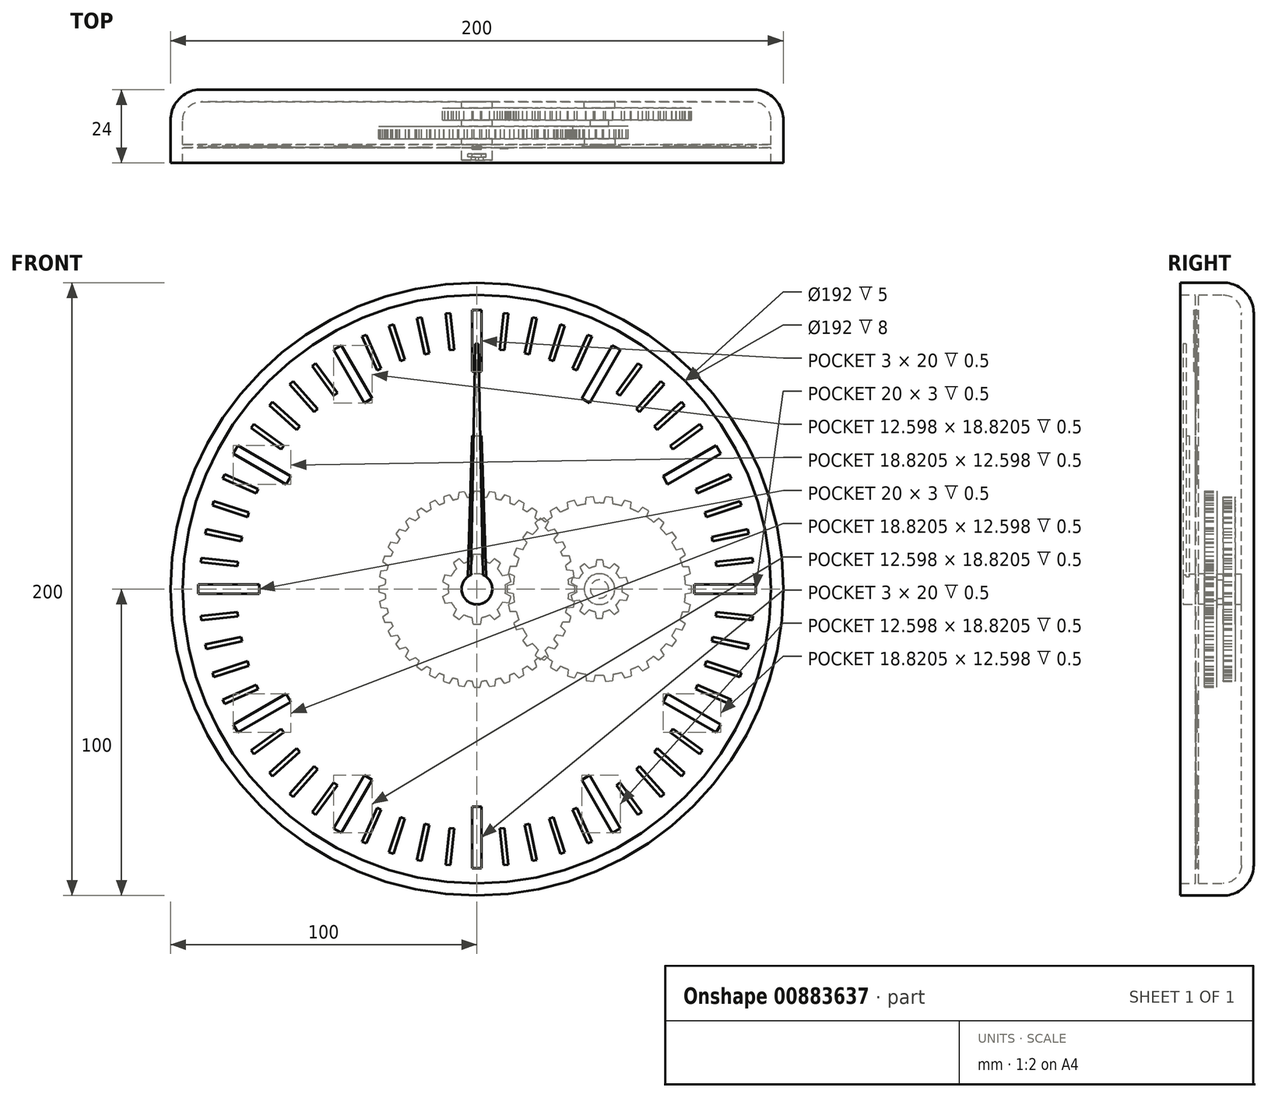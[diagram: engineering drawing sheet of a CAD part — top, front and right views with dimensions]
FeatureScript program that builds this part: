
annotation { "Feature Type Name" : "Feature", "Feature Type Description" : "" }
export const myFeature = defineFeature(function(context is Context, id is Id, definition is map)
    precondition{}
    {
        {
            var Q0;
            Q0=qCreatedBy(makeId("Front.planeOp"),FACE);
            var sketch = newSketch(context, id + "F0", { "sketchPlane" : qUnion([Q0])});
            skCircle(sketch, "E0", {"center": v(0, 0) * mm, "radius": 100 * mm});
            skSolve(sketch);
        }
        {
            var Q0;
            Q0 = qSketchRegion(id + "F0", true);
            extrude(context, id + "F1", {"entities" : qUnion([Q0]), "depth" : 24 * mm, "offsetDistance" : 25 * mm});
        }
        {
            var Q0;
            Q0=makeQuery(id+"F1.opExtrude","CAP_EDGE",EDGE,{"disambiguationData":[OSD([sQuery(id+"F0.wireOp",EDGE,"E0")])],"isStart":true});
            fillet(context, id + "F2", {"entities" : qUnion([Q0]), "radius" : 10 * mm, "tangentPropagation" : true, "allowEdgeOverflow" : false});
        }
        {
            var Q0;
            Q0=makeQuery(id+"F1.opExtrude","CAP_FACE",FACE,{"disambiguationData":[OSD([sQuery(id+"F0.wireOp",EDGE,"E0")])],"isStart":false});
            shell(context, id + "F3", {"entities" : qUnion([Q0]), "thickness" : 4 * mm});
        }
        {
            var Q0;
            {var subQ0=sQuery(id+"F0.wireOp",EDGE,"E0");Q0=makeQuery(id+"F3.opShell","OFFSET_FACE",FACE,{"disambiguationData":[OSD([subQ0]),TDD([makeQuery(id+"F1.opExtrude","CAP_FACE",FACE,{"disambiguationData":[OSD([subQ0])],"isStart":true})])]});}
            var sketch = newSketch(context, id + "F4", { "sketchPlane" : qUnion([Q0])});
            skCircle(sketch, "E1", {"center": v(0, 0) * mm, "radius": 5 * mm});
            skCircle(sketch, "E2", {"center": v(0, 0) * mm, "radius": 3 * mm});
            skCircle(sketch, "E3", {"center": v(40, 0) * mm, "radius": 5 * mm});
            skCircle(sketch, "E4", {"center": v(40, 0) * mm, "radius": 3 * mm});
            skSolve(sketch);
        }
        {
            var Q0;
            Q0 = qSketchRegion(id + "F4", true);
            extrude(context, id + "F5", {"entities" : qUnion([Q0]), "operationType" : NewBodyOperationType.ADD, "depth" : 2 * mm, "offsetDistance" : 25 * mm});
        }
        {
            var Q0;
            {var subQ0=sQuery(id+"F0.wireOp",EDGE,"E0");Q0=makeQuery(id+"F5.boolean.opBoolean","SPLIT",FACE,{"disambiguationData":[TD([makeQuery(id+"F5.opExtrude","SWEPT_FACE",FACE,{"disambiguationData":[OSD([sQuery(id+"F4.wireOp",EDGE,"E2")])]})])],"derivedFrom":makeQuery(id+"F3.opShell","OFFSET_FACE",FACE,{"disambiguationData":[OSD([subQ0]),TDD([makeQuery(id+"F1.opExtrude","CAP_FACE",FACE,{"disambiguationData":[OSD([subQ0])],"isStart":true})])]})});}
            extrude(context, id + "F6", {"entities" : qUnion([Q0]), "depth" : 19 * mm, "offsetDistance" : 25 * mm});
        }
        {
            var Q0;
            {var subQ0=sQuery(id+"F0.wireOp",EDGE,"E0");Q0=makeQuery(id+"F5.boolean.opBoolean","SPLIT",FACE,{"disambiguationData":[TD([makeQuery(id+"F5.opExtrude","SWEPT_FACE",FACE,{"disambiguationData":[OSD([sQuery(id+"F4.wireOp",EDGE,"E4")])]})])],"derivedFrom":makeQuery(id+"F3.opShell","OFFSET_FACE",FACE,{"disambiguationData":[OSD([subQ0]),TDD([makeQuery(id+"F1.opExtrude","CAP_FACE",FACE,{"disambiguationData":[OSD([subQ0])],"isStart":true})])]})});}
            extrude(context, id + "F7", {"entities" : qUnion([Q0]), "depth" : 8 * mm, "offsetDistance" : 25 * mm});
        }
        {
            var Q0;
            Q0=makeQuery(id+"F5.opExtrude","CAP_FACE",FACE,{"disambiguationData":[OSD([sQuery(id+"F4.wireOp",EDGE,"E1"),sQuery(id+"F4.wireOp",EDGE,"E2")])],"isStart":false});
            var sketch = newSketch(context, id + "F8", { "sketchPlane" : qUnion([Q0])});
            skCircle(sketch, "E5", {"center": v(0, 0) * mm, "radius": 9.38 * mm});
            skLineSegment(sketch, "E6", {"start": v(0, 11.38) * mm, "end": v(1.18, 11.38) * mm});
            skLineSegment(sketch, "E7", {"start": v(1.18, 11.38) * mm, "end": v(1.55, 9.25) * mm});
            skLineSegment(sketch, "E8.MirrorCS", {"start": v(0, 11.38) * mm, "end": v(-1.18, 11.38) * mm});
            skLineSegment(sketch, "E9.MirrorCS", {"start": v(-1.18, 11.38) * mm, "end": v(-1.55, 9.25) * mm});
            skLineSegment(sketch, "E10.1.0", {"start": v(-7.64, 8.51) * mm, "end": v(-6.7, 6.57) * mm});
            skLineSegment(sketch, "E10.1.1", {"start": v(-6.69, 9.2) * mm, "end": v(-7.64, 8.51) * mm});
            skLineSegment(sketch, "E10.1.2", {"start": v(-6.69, 9.2) * mm, "end": v(-5.73, 9.9) * mm});
            skLineSegment(sketch, "E10.1.3", {"start": v(-5.73, 9.9) * mm, "end": v(-4.18, 8.4) * mm});
            skLineSegment(sketch, "E10.2.0", {"start": v(-11.18, 2.4) * mm, "end": v(-9.27, 1.38) * mm});
            skLineSegment(sketch, "E10.2.1", {"start": v(-10.82, 3.52) * mm, "end": v(-11.18, 2.4) * mm});
            skLineSegment(sketch, "E10.2.2", {"start": v(-10.82, 3.52) * mm, "end": v(-10.45, 4.64) * mm});
            skLineSegment(sketch, "E10.2.3", {"start": v(-10.45, 4.64) * mm, "end": v(-8.31, 4.33) * mm});
            skLineSegment(sketch, "E11.2.3.0", {"start": v(-10.45, -4.64) * mm, "end": v(-8.31, -4.33) * mm});
            skLineSegment(sketch, "E11.3.3.0", {"start": v(-10.82, -3.52) * mm, "end": v(-10.45, -4.64) * mm});
            skLineSegment(sketch, "E11.6.3.0", {"start": v(-10.82, -3.52) * mm, "end": v(-11.18, -2.4) * mm});
            skLineSegment(sketch, "E11.9.3.0", {"start": v(-11.18, -2.4) * mm, "end": v(-9.27, -1.38) * mm});
            skLineSegment(sketch, "E11.2.4.0", {"start": v(-5.73, -9.9) * mm, "end": v(-4.18, -8.4) * mm});
            skLineSegment(sketch, "E11.3.4.0", {"start": v(-6.69, -9.2) * mm, "end": v(-5.73, -9.9) * mm});
            skLineSegment(sketch, "E11.6.4.0", {"start": v(-6.69, -9.2) * mm, "end": v(-7.64, -8.51) * mm});
            skLineSegment(sketch, "E11.9.4.0", {"start": v(-7.64, -8.51) * mm, "end": v(-6.7, -6.57) * mm});
            skLineSegment(sketch, "E11.2.5.0", {"start": v(1.18, -11.38) * mm, "end": v(1.55, -9.25) * mm});
            skLineSegment(sketch, "E11.3.5.0", {"start": v(0, -11.38) * mm, "end": v(1.18, -11.38) * mm});
            skLineSegment(sketch, "E11.6.5.0", {"start": v(0, -11.38) * mm, "end": v(-1.18, -11.38) * mm});
            skLineSegment(sketch, "E11.9.5.0", {"start": v(-1.18, -11.38) * mm, "end": v(-1.55, -9.25) * mm});
            skLineSegment(sketch, "E11.2.6.0", {"start": v(7.64, -8.51) * mm, "end": v(6.7, -6.57) * mm});
            skLineSegment(sketch, "E11.3.6.0", {"start": v(6.69, -9.2) * mm, "end": v(7.64, -8.51) * mm});
            skLineSegment(sketch, "E11.6.6.0", {"start": v(6.69, -9.2) * mm, "end": v(5.73, -9.9) * mm});
            skLineSegment(sketch, "E11.9.6.0", {"start": v(5.73, -9.9) * mm, "end": v(4.18, -8.4) * mm});
            skLineSegment(sketch, "E11.2.7.0", {"start": v(11.18, -2.4) * mm, "end": v(9.27, -1.38) * mm});
            skLineSegment(sketch, "E11.3.7.0", {"start": v(10.82, -3.52) * mm, "end": v(11.18, -2.4) * mm});
            skLineSegment(sketch, "E11.6.7.0", {"start": v(10.82, -3.52) * mm, "end": v(10.45, -4.64) * mm});
            skLineSegment(sketch, "E11.9.7.0", {"start": v(10.45, -4.64) * mm, "end": v(8.31, -4.33) * mm});
            skLineSegment(sketch, "E11.2.8.0", {"start": v(10.45, 4.64) * mm, "end": v(8.31, 4.33) * mm});
            skLineSegment(sketch, "E11.3.8.0", {"start": v(10.82, 3.52) * mm, "end": v(10.45, 4.64) * mm});
            skLineSegment(sketch, "E11.6.8.0", {"start": v(10.82, 3.52) * mm, "end": v(11.18, 2.4) * mm});
            skLineSegment(sketch, "E11.9.8.0", {"start": v(11.18, 2.4) * mm, "end": v(9.27, 1.38) * mm});
            skLineSegment(sketch, "E11.2.9.0", {"start": v(5.73, 9.9) * mm, "end": v(4.18, 8.4) * mm});
            skLineSegment(sketch, "E11.3.9.0", {"start": v(6.69, 9.2) * mm, "end": v(5.73, 9.9) * mm});
            skLineSegment(sketch, "E11.6.9.0", {"start": v(6.69, 9.2) * mm, "end": v(7.64, 8.51) * mm});
            skLineSegment(sketch, "E11.9.9.0", {"start": v(7.64, 8.51) * mm, "end": v(6.7, 6.57) * mm});
            skSolve(sketch);
        }
        {
            var Q0;
            Q0 = qSketchRegion(id + "F8", true);
            extrude(context, id + "F9", {"entities" : qUnion([Q0]), "operationType" : NewBodyOperationType.ADD, "depth" : 4 * mm, "offsetDistance" : 25 * mm});
        }
        {
            var Q0;
            Q0=makeQuery(id+"F5.opExtrude","CAP_FACE",FACE,{"disambiguationData":[OSD([sQuery(id+"F4.wireOp",EDGE,"E3"),sQuery(id+"F4.wireOp",EDGE,"E4")])],"isStart":false});
            var sketch = newSketch(context, id + "F10", { "sketchPlane" : qUnion([Q0])});
            skCircle(sketch, "E12", {"center": v(40, 0) * mm, "radius": 28.13 * mm});
            skLineSegment(sketch, "E13", {"start": v(11.92, 1.54) * mm, "end": v(9.88, 1.18) * mm});
            skLineSegment(sketch, "E14", {"start": v(9.88, 1.18) * mm, "end": v(9.88, 0) * mm});
            skLineSegment(sketch, "E15.MirrorCS", {"start": v(9.88, -1.18) * mm, "end": v(9.88, 0) * mm});
            skLineSegment(sketch, "E16.MirrorCS", {"start": v(11.92, -1.54) * mm, "end": v(9.88, -1.18) * mm});
            skLineSegment(sketch, "E17.1.0", {"start": v(12.21, -4.33) * mm, "end": v(10.29, -5.11) * mm});
            skLineSegment(sketch, "E17.1.1", {"start": v(10.29, -5.11) * mm, "end": v(10.53, -6.26) * mm});
            skLineSegment(sketch, "E17.1.2", {"start": v(10.78, -7.42) * mm, "end": v(10.53, -6.26) * mm});
            skLineSegment(sketch, "E17.1.3", {"start": v(12.85, -7.34) * mm, "end": v(10.78, -7.42) * mm});
            skLineSegment(sketch, "E17.2.0", {"start": v(13.72, -10.02) * mm, "end": v(12, -11.18) * mm});
            skLineSegment(sketch, "E17.2.1", {"start": v(12, -11.18) * mm, "end": v(12.48, -12.25) * mm});
            skLineSegment(sketch, "E17.2.2", {"start": v(12.96, -13.33) * mm, "end": v(12.48, -12.25) * mm});
            skLineSegment(sketch, "E17.2.3", {"start": v(14.97, -12.83) * mm, "end": v(12.96, -13.33) * mm});
            skLineSegment(sketch, "E18.2.3.0", {"start": v(16.38, -15.26) * mm, "end": v(14.94, -16.75) * mm});
            skLineSegment(sketch, "E18.3.3.0", {"start": v(14.94, -16.75) * mm, "end": v(15.63, -17.7) * mm});
            skLineSegment(sketch, "E18.6.3.0", {"start": v(16.32, -18.66) * mm, "end": v(15.63, -17.7) * mm});
            skLineSegment(sketch, "E18.9.3.0", {"start": v(18.18, -17.75) * mm, "end": v(16.32, -18.66) * mm});
            skLineSegment(sketch, "E18.2.4.0", {"start": v(20.07, -19.84) * mm, "end": v(18.97, -21.6) * mm});
            skLineSegment(sketch, "E18.3.4.0", {"start": v(18.97, -21.6) * mm, "end": v(19.84, -22.39) * mm});
            skLineSegment(sketch, "E18.6.4.0", {"start": v(20.72, -23.18) * mm, "end": v(19.84, -22.39) * mm});
            skLineSegment(sketch, "E18.9.4.0", {"start": v(22.35, -21.9) * mm, "end": v(20.72, -23.18) * mm});
            skLineSegment(sketch, "E18.2.5.0", {"start": v(24.63, -23.55) * mm, "end": v(23.92, -25.5) * mm});
            skLineSegment(sketch, "E18.3.5.0", {"start": v(23.92, -25.5) * mm, "end": v(24.94, -26.09) * mm});
            skLineSegment(sketch, "E18.6.5.0", {"start": v(25.96, -26.68) * mm, "end": v(24.94, -26.09) * mm});
            skLineSegment(sketch, "E18.9.5.0", {"start": v(27.3, -25.09) * mm, "end": v(25.96, -26.68) * mm});
            skLineSegment(sketch, "E18.2.6.0", {"start": v(29.86, -26.23) * mm, "end": v(29.57, -28.29) * mm});
            skLineSegment(sketch, "E18.3.6.0", {"start": v(29.57, -28.29) * mm, "end": v(30.7, -28.65) * mm});
            skLineSegment(sketch, "E18.6.6.0", {"start": v(31.81, -29.01) * mm, "end": v(30.7, -28.65) * mm});
            skLineSegment(sketch, "E18.9.6.0", {"start": v(32.78, -27.18) * mm, "end": v(31.81, -29.01) * mm});
            skLineSegment(sketch, "E18.2.7.0", {"start": v(35.53, -27.77) * mm, "end": v(35.68, -29.84) * mm});
            skLineSegment(sketch, "E18.3.7.0", {"start": v(35.68, -29.84) * mm, "end": v(36.85, -29.96) * mm});
            skLineSegment(sketch, "E18.6.7.0", {"start": v(38.02, -30.08) * mm, "end": v(36.85, -29.96) * mm});
            skLineSegment(sketch, "E18.9.7.0", {"start": v(38.6, -28.09) * mm, "end": v(38.02, -30.08) * mm});
            skLineSegment(sketch, "E18.2.8.0", {"start": v(41.4, -28.09) * mm, "end": v(41.98, -30.08) * mm});
            skLineSegment(sketch, "E18.3.8.0", {"start": v(41.98, -30.08) * mm, "end": v(43.15, -29.96) * mm});
            skLineSegment(sketch, "E18.6.8.0", {"start": v(44.32, -29.84) * mm, "end": v(43.15, -29.96) * mm});
            skLineSegment(sketch, "E18.9.8.0", {"start": v(44.47, -27.77) * mm, "end": v(44.32, -29.84) * mm});
            skLineSegment(sketch, "E18.2.9.0", {"start": v(47.22, -27.18) * mm, "end": v(48.19, -29.01) * mm});
            skLineSegment(sketch, "E18.3.9.0", {"start": v(48.19, -29.01) * mm, "end": v(49.3, -28.65) * mm});
            skLineSegment(sketch, "E18.6.9.0", {"start": v(50.43, -28.29) * mm, "end": v(49.3, -28.65) * mm});
            skLineSegment(sketch, "E18.9.9.0", {"start": v(50.14, -26.23) * mm, "end": v(50.43, -28.29) * mm});
            skLineSegment(sketch, "E18.2.10.0", {"start": v(52.7, -25.09) * mm, "end": v(54.04, -26.68) * mm});
            skLineSegment(sketch, "E18.3.10.0", {"start": v(54.04, -26.68) * mm, "end": v(55.06, -26.09) * mm});
            skLineSegment(sketch, "E18.6.10.0", {"start": v(56.08, -25.5) * mm, "end": v(55.06, -26.09) * mm});
            skLineSegment(sketch, "E18.9.10.0", {"start": v(55.37, -23.55) * mm, "end": v(56.08, -25.5) * mm});
            skLineSegment(sketch, "E18.2.11.0", {"start": v(57.65, -21.9) * mm, "end": v(59.28, -23.18) * mm});
            skLineSegment(sketch, "E18.3.11.0", {"start": v(59.28, -23.18) * mm, "end": v(60.16, -22.39) * mm});
            skLineSegment(sketch, "E18.6.11.0", {"start": v(61.03, -21.6) * mm, "end": v(60.16, -22.39) * mm});
            skLineSegment(sketch, "E18.9.11.0", {"start": v(59.93, -19.84) * mm, "end": v(61.03, -21.6) * mm});
            skLineSegment(sketch, "E18.2.12.0", {"start": v(61.82, -17.75) * mm, "end": v(63.68, -18.66) * mm});
            skLineSegment(sketch, "E18.3.12.0", {"start": v(63.68, -18.66) * mm, "end": v(64.37, -17.7) * mm});
            skLineSegment(sketch, "E18.6.12.0", {"start": v(65.06, -16.75) * mm, "end": v(64.37, -17.7) * mm});
            skLineSegment(sketch, "E18.9.12.0", {"start": v(63.62, -15.26) * mm, "end": v(65.06, -16.75) * mm});
            skLineSegment(sketch, "E18.2.13.0", {"start": v(65.03, -12.83) * mm, "end": v(67.04, -13.33) * mm});
            skLineSegment(sketch, "E18.3.13.0", {"start": v(67.04, -13.33) * mm, "end": v(67.52, -12.25) * mm});
            skLineSegment(sketch, "E18.6.13.0", {"start": v(68, -11.18) * mm, "end": v(67.52, -12.25) * mm});
            skLineSegment(sketch, "E18.9.13.0", {"start": v(66.28, -10.02) * mm, "end": v(68, -11.18) * mm});
            skLineSegment(sketch, "E18.2.14.0", {"start": v(67.15, -7.34) * mm, "end": v(69.22, -7.42) * mm});
            skLineSegment(sketch, "E18.3.14.0", {"start": v(69.22, -7.42) * mm, "end": v(69.47, -6.26) * mm});
            skLineSegment(sketch, "E18.6.14.0", {"start": v(69.71, -5.11) * mm, "end": v(69.47, -6.26) * mm});
            skLineSegment(sketch, "E18.9.14.0", {"start": v(67.79, -4.33) * mm, "end": v(69.71, -5.11) * mm});
            skLineSegment(sketch, "E18.2.15.0", {"start": v(68.08, -1.54) * mm, "end": v(70.12, -1.18) * mm});
            skLineSegment(sketch, "E18.3.15.0", {"start": v(70.12, -1.18) * mm, "end": v(70.12, 0) * mm});
            skLineSegment(sketch, "E18.6.15.0", {"start": v(70.12, 1.18) * mm, "end": v(70.12, 0) * mm});
            skLineSegment(sketch, "E18.9.15.0", {"start": v(68.08, 1.54) * mm, "end": v(70.12, 1.18) * mm});
            skLineSegment(sketch, "E18.2.16.0", {"start": v(67.79, 4.33) * mm, "end": v(69.71, 5.11) * mm});
            skLineSegment(sketch, "E18.3.16.0", {"start": v(69.71, 5.11) * mm, "end": v(69.47, 6.26) * mm});
            skLineSegment(sketch, "E18.6.16.0", {"start": v(69.22, 7.42) * mm, "end": v(69.47, 6.26) * mm});
            skLineSegment(sketch, "E18.9.16.0", {"start": v(67.15, 7.34) * mm, "end": v(69.22, 7.42) * mm});
            skLineSegment(sketch, "E18.2.17.0", {"start": v(66.28, 10.02) * mm, "end": v(68, 11.18) * mm});
            skLineSegment(sketch, "E18.3.17.0", {"start": v(68, 11.18) * mm, "end": v(67.52, 12.25) * mm});
            skLineSegment(sketch, "E18.6.17.0", {"start": v(67.04, 13.33) * mm, "end": v(67.52, 12.25) * mm});
            skLineSegment(sketch, "E18.9.17.0", {"start": v(65.03, 12.83) * mm, "end": v(67.04, 13.33) * mm});
            skLineSegment(sketch, "E18.2.18.0", {"start": v(63.62, 15.26) * mm, "end": v(65.06, 16.75) * mm});
            skLineSegment(sketch, "E18.3.18.0", {"start": v(65.06, 16.75) * mm, "end": v(64.37, 17.7) * mm});
            skLineSegment(sketch, "E18.6.18.0", {"start": v(63.68, 18.66) * mm, "end": v(64.37, 17.7) * mm});
            skLineSegment(sketch, "E18.9.18.0", {"start": v(61.82, 17.75) * mm, "end": v(63.68, 18.66) * mm});
            skLineSegment(sketch, "E18.2.19.0", {"start": v(59.93, 19.84) * mm, "end": v(61.03, 21.6) * mm});
            skLineSegment(sketch, "E18.3.19.0", {"start": v(61.03, 21.6) * mm, "end": v(60.16, 22.39) * mm});
            skLineSegment(sketch, "E18.6.19.0", {"start": v(59.28, 23.18) * mm, "end": v(60.16, 22.39) * mm});
            skLineSegment(sketch, "E18.9.19.0", {"start": v(57.65, 21.9) * mm, "end": v(59.28, 23.18) * mm});
            skLineSegment(sketch, "E18.2.20.0", {"start": v(55.37, 23.55) * mm, "end": v(56.08, 25.5) * mm});
            skLineSegment(sketch, "E18.3.20.0", {"start": v(56.08, 25.5) * mm, "end": v(55.06, 26.09) * mm});
            skLineSegment(sketch, "E18.6.20.0", {"start": v(54.04, 26.68) * mm, "end": v(55.06, 26.09) * mm});
            skLineSegment(sketch, "E18.9.20.0", {"start": v(52.7, 25.09) * mm, "end": v(54.04, 26.68) * mm});
            skLineSegment(sketch, "E18.2.21.0", {"start": v(50.14, 26.23) * mm, "end": v(50.43, 28.29) * mm});
            skLineSegment(sketch, "E18.3.21.0", {"start": v(50.43, 28.29) * mm, "end": v(49.3, 28.65) * mm});
            skLineSegment(sketch, "E18.6.21.0", {"start": v(48.19, 29.01) * mm, "end": v(49.3, 28.65) * mm});
            skLineSegment(sketch, "E18.9.21.0", {"start": v(47.22, 27.18) * mm, "end": v(48.19, 29.01) * mm});
            skLineSegment(sketch, "E18.2.22.0", {"start": v(44.47, 27.77) * mm, "end": v(44.32, 29.84) * mm});
            skLineSegment(sketch, "E18.3.22.0", {"start": v(44.32, 29.84) * mm, "end": v(43.15, 29.96) * mm});
            skLineSegment(sketch, "E18.6.22.0", {"start": v(41.98, 30.08) * mm, "end": v(43.15, 29.96) * mm});
            skLineSegment(sketch, "E18.9.22.0", {"start": v(41.4, 28.09) * mm, "end": v(41.98, 30.08) * mm});
            skLineSegment(sketch, "E18.2.23.0", {"start": v(38.6, 28.09) * mm, "end": v(38.02, 30.08) * mm});
            skLineSegment(sketch, "E18.3.23.0", {"start": v(38.02, 30.08) * mm, "end": v(36.85, 29.96) * mm});
            skLineSegment(sketch, "E18.6.23.0", {"start": v(35.68, 29.84) * mm, "end": v(36.85, 29.96) * mm});
            skLineSegment(sketch, "E18.9.23.0", {"start": v(35.53, 27.77) * mm, "end": v(35.68, 29.84) * mm});
            skLineSegment(sketch, "E18.2.24.0", {"start": v(32.78, 27.18) * mm, "end": v(31.81, 29.01) * mm});
            skLineSegment(sketch, "E18.3.24.0", {"start": v(31.81, 29.01) * mm, "end": v(30.7, 28.65) * mm});
            skLineSegment(sketch, "E18.6.24.0", {"start": v(29.57, 28.29) * mm, "end": v(30.7, 28.65) * mm});
            skLineSegment(sketch, "E18.9.24.0", {"start": v(29.86, 26.23) * mm, "end": v(29.57, 28.29) * mm});
            skLineSegment(sketch, "E18.2.25.0", {"start": v(27.3, 25.09) * mm, "end": v(25.96, 26.68) * mm});
            skLineSegment(sketch, "E18.3.25.0", {"start": v(25.96, 26.68) * mm, "end": v(24.94, 26.09) * mm});
            skLineSegment(sketch, "E18.6.25.0", {"start": v(23.92, 25.5) * mm, "end": v(24.94, 26.09) * mm});
            skLineSegment(sketch, "E18.9.25.0", {"start": v(24.63, 23.55) * mm, "end": v(23.92, 25.5) * mm});
            skLineSegment(sketch, "E18.2.26.0", {"start": v(22.35, 21.9) * mm, "end": v(20.72, 23.18) * mm});
            skLineSegment(sketch, "E18.3.26.0", {"start": v(20.72, 23.18) * mm, "end": v(19.84, 22.39) * mm});
            skLineSegment(sketch, "E18.6.26.0", {"start": v(18.97, 21.6) * mm, "end": v(19.84, 22.39) * mm});
            skLineSegment(sketch, "E18.9.26.0", {"start": v(20.07, 19.84) * mm, "end": v(18.97, 21.6) * mm});
            skLineSegment(sketch, "E18.2.27.0", {"start": v(18.18, 17.75) * mm, "end": v(16.32, 18.66) * mm});
            skLineSegment(sketch, "E18.3.27.0", {"start": v(16.32, 18.66) * mm, "end": v(15.63, 17.7) * mm});
            skLineSegment(sketch, "E18.6.27.0", {"start": v(14.94, 16.75) * mm, "end": v(15.63, 17.7) * mm});
            skLineSegment(sketch, "E18.9.27.0", {"start": v(16.38, 15.26) * mm, "end": v(14.94, 16.75) * mm});
            skLineSegment(sketch, "E18.2.28.0", {"start": v(14.97, 12.83) * mm, "end": v(12.96, 13.33) * mm});
            skLineSegment(sketch, "E18.3.28.0", {"start": v(12.96, 13.33) * mm, "end": v(12.48, 12.25) * mm});
            skLineSegment(sketch, "E18.6.28.0", {"start": v(12, 11.18) * mm, "end": v(12.48, 12.25) * mm});
            skLineSegment(sketch, "E18.9.28.0", {"start": v(13.72, 10.02) * mm, "end": v(12, 11.18) * mm});
            skLineSegment(sketch, "E18.2.29.0", {"start": v(12.85, 7.34) * mm, "end": v(10.78, 7.42) * mm});
            skLineSegment(sketch, "E18.3.29.0", {"start": v(10.78, 7.42) * mm, "end": v(10.53, 6.26) * mm});
            skLineSegment(sketch, "E18.6.29.0", {"start": v(10.29, 5.11) * mm, "end": v(10.53, 6.26) * mm});
            skLineSegment(sketch, "E18.9.29.0", {"start": v(12.21, 4.33) * mm, "end": v(10.29, 5.11) * mm});
            skSolve(sketch);
        }
        {
            var Q0;
            Q0 = qSketchRegion(id + "F10", true);
            extrude(context, id + "F11", {"entities" : qUnion([Q0]), "operationType" : NewBodyOperationType.ADD, "depth" : 4 * mm, "offsetDistance" : 25 * mm});
        }
        {
            var Q0;
            Q0=makeQuery(id+"F9.opExtrude","CAP_FACE",FACE,{"disambiguationData":[OSD([sQuery(id+"F8.wireOp",EDGE,"E5"),sQuery(id+"F8.wireOp",EDGE,"E6"),sQuery(id+"F8.wireOp",EDGE,"E7"),sQuery(id+"F8.wireOp",EDGE,"E8.MirrorCS"),sQuery(id+"F8.wireOp",EDGE,"E9.MirrorCS"),sQuery(id+"F8.wireOp",EDGE,"E10.1.0"),sQuery(id+"F8.wireOp",EDGE,"E10.1.1"),sQuery(id+"F8.wireOp",EDGE,"E10.1.2"),sQuery(id+"F8.wireOp",EDGE,"E10.1.3"),sQuery(id+"F8.wireOp",EDGE,"E10.2.0"),sQuery(id+"F8.wireOp",EDGE,"E10.2.1"),sQuery(id+"F8.wireOp",EDGE,"E10.2.2"),sQuery(id+"F8.wireOp",EDGE,"E10.2.3"),sQuery(id+"F8.wireOp",EDGE,"E11.2.3.0"),sQuery(id+"F8.wireOp",EDGE,"E11.3.3.0"),sQuery(id+"F8.wireOp",EDGE,"E11.6.3.0"),sQuery(id+"F8.wireOp",EDGE,"E11.9.3.0"),sQuery(id+"F8.wireOp",EDGE,"E11.2.4.0"),sQuery(id+"F8.wireOp",EDGE,"E11.3.4.0"),sQuery(id+"F8.wireOp",EDGE,"E11.6.4.0"),sQuery(id+"F8.wireOp",EDGE,"E11.9.4.0"),sQuery(id+"F8.wireOp",EDGE,"E11.2.5.0"),sQuery(id+"F8.wireOp",EDGE,"E11.3.5.0"),sQuery(id+"F8.wireOp",EDGE,"E11.6.5.0"),sQuery(id+"F8.wireOp",EDGE,"E11.9.5.0"),sQuery(id+"F8.wireOp",EDGE,"E11.2.6.0"),sQuery(id+"F8.wireOp",EDGE,"E11.3.6.0"),sQuery(id+"F8.wireOp",EDGE,"E11.6.6.0"),sQuery(id+"F8.wireOp",EDGE,"E11.9.6.0"),sQuery(id+"F8.wireOp",EDGE,"E11.2.7.0"),sQuery(id+"F8.wireOp",EDGE,"E11.3.7.0"),sQuery(id+"F8.wireOp",EDGE,"E11.6.7.0"),sQuery(id+"F8.wireOp",EDGE,"E11.9.7.0"),sQuery(id+"F8.wireOp",EDGE,"E11.2.8.0"),sQuery(id+"F8.wireOp",EDGE,"E11.3.8.0"),sQuery(id+"F8.wireOp",EDGE,"E11.6.8.0"),sQuery(id+"F8.wireOp",EDGE,"E11.9.8.0"),sQuery(id+"F8.wireOp",EDGE,"E11.2.9.0"),sQuery(id+"F8.wireOp",EDGE,"E11.3.9.0"),sQuery(id+"F8.wireOp",EDGE,"E11.6.9.0"),sQuery(id+"F8.wireOp",EDGE,"E11.9.9.0")])],"isStart":false});
            var sketch = newSketch(context, id + "F12", { "sketchPlane" : qUnion([Q0])});
            skCircle(sketch, "E19.0", {"center": v(0, 0) * mm, "radius": 3 * mm});
            skCircle(sketch, "E20.0", {"center": v(0, 0) * mm, "radius": 5 * mm});
            skSolve(sketch);
        }
        {
            var Q0;
            Q0 = qSketchRegion(id + "F12", true);
            extrude(context, id + "F13", {"entities" : qUnion([Q0]), "depth" : 2 * mm, "offsetDistance" : 25 * mm});
        }
        {
            var Q0;
            Q0=makeQuery(id+"F13.opExtrude","CAP_FACE",FACE,{"disambiguationData":[OSD([sQuery(id+"F12.wireOp",EDGE,"E19.0"),sQuery(id+"F12.wireOp",EDGE,"E20.0")])],"isStart":false});
            var sketch = newSketch(context, id + "F14", { "sketchPlane" : qUnion([Q0])});
            skCircle(sketch, "E21.0", {"center": v(0, 0) * mm, "radius": 3 * mm});
            skCircle(sketch, "E22", {"center": v(0, 0) * mm, "radius": 30 * mm});
            skLineSegment(sketch, "E23", {"start": v(0, 32) * mm, "end": v(0.94, 32) * mm});
            skLineSegment(sketch, "E24", {"start": v(0.94, 32) * mm, "end": v(1.58, 29.96) * mm});
            skLineSegment(sketch, "E25.MirrorCS", {"start": v(0, 32) * mm, "end": v(-0.94, 32) * mm});
            skLineSegment(sketch, "E26.MirrorCS", {"start": v(-0.94, 32) * mm, "end": v(-1.58, 29.96) * mm});
            skLineSegment(sketch, "E27.1.0", {"start": v(-5.94, 31.46) * mm, "end": v(-6.25, 29.34) * mm});
            skLineSegment(sketch, "E27.1.1", {"start": v(-5, 31.6) * mm, "end": v(-5.94, 31.46) * mm});
            skLineSegment(sketch, "E27.1.2", {"start": v(-5, 31.6) * mm, "end": v(-4.08, 31.75) * mm});
            skLineSegment(sketch, "E27.1.3", {"start": v(-4.08, 31.75) * mm, "end": v(-3.13, 29.84) * mm});
            skLineSegment(sketch, "E27.2.0", {"start": v(-10.78, 30.14) * mm, "end": v(-10.76, 28) * mm});
            skLineSegment(sketch, "E27.2.1", {"start": v(-9.89, 30.43) * mm, "end": v(-10.78, 30.14) * mm});
            skLineSegment(sketch, "E27.2.2", {"start": v(-9.89, 30.43) * mm, "end": v(-9, 30.73) * mm});
            skLineSegment(sketch, "E27.2.3", {"start": v(-9, 30.73) * mm, "end": v(-7.75, 28.98) * mm});
            skLineSegment(sketch, "E28.2.3.0", {"start": v(-15.37, 28.08) * mm, "end": v(-15, 25.98) * mm});
            skLineSegment(sketch, "E28.3.3.0", {"start": v(-14.53, 28.51) * mm, "end": v(-15.37, 28.08) * mm});
            skLineSegment(sketch, "E28.6.3.0", {"start": v(-14.53, 28.51) * mm, "end": v(-13.69, 28.94) * mm});
            skLineSegment(sketch, "E28.9.3.0", {"start": v(-13.69, 28.94) * mm, "end": v(-12.2, 27.41) * mm});
            skLineSegment(sketch, "E28.2.4.0", {"start": v(-19.57, 25.33) * mm, "end": v(-18.89, 23.3) * mm});
            skLineSegment(sketch, "E28.3.4.0", {"start": v(-18.8, 25.89) * mm, "end": v(-19.57, 25.33) * mm});
            skLineSegment(sketch, "E28.6.4.0", {"start": v(-18.8, 25.89) * mm, "end": v(-18.05, 26.44) * mm});
            skLineSegment(sketch, "E28.9.4.0", {"start": v(-18.05, 26.44) * mm, "end": v(-16.33, 25.17) * mm});
            skLineSegment(sketch, "E28.2.5.0", {"start": v(-23.3, 21.96) * mm, "end": v(-22.3, 20.07) * mm});
            skLineSegment(sketch, "E28.3.5.0", {"start": v(-22.63, 22.63) * mm, "end": v(-23.3, 21.96) * mm});
            skLineSegment(sketch, "E28.6.5.0", {"start": v(-22.63, 22.63) * mm, "end": v(-21.96, 23.3) * mm});
            skLineSegment(sketch, "E28.9.5.0", {"start": v(-21.96, 23.3) * mm, "end": v(-20.07, 22.3) * mm});
            skLineSegment(sketch, "E28.2.6.0", {"start": v(-26.44, 18.05) * mm, "end": v(-25.17, 16.33) * mm});
            skLineSegment(sketch, "E28.3.6.0", {"start": v(-25.89, 18.8) * mm, "end": v(-26.44, 18.05) * mm});
            skLineSegment(sketch, "E28.6.6.0", {"start": v(-25.89, 18.8) * mm, "end": v(-25.33, 19.57) * mm});
            skLineSegment(sketch, "E28.9.6.0", {"start": v(-25.33, 19.57) * mm, "end": v(-23.3, 18.89) * mm});
            skLineSegment(sketch, "E28.2.7.0", {"start": v(-28.94, 13.69) * mm, "end": v(-27.41, 12.2) * mm});
            skLineSegment(sketch, "E28.3.7.0", {"start": v(-28.51, 14.53) * mm, "end": v(-28.94, 13.69) * mm});
            skLineSegment(sketch, "E28.6.7.0", {"start": v(-28.51, 14.53) * mm, "end": v(-28.08, 15.37) * mm});
            skLineSegment(sketch, "E28.9.7.0", {"start": v(-28.08, 15.37) * mm, "end": v(-25.98, 15) * mm});
            skLineSegment(sketch, "E28.2.8.0", {"start": v(-30.73, 9) * mm, "end": v(-28.98, 7.75) * mm});
            skLineSegment(sketch, "E28.3.8.0", {"start": v(-30.43, 9.89) * mm, "end": v(-30.73, 9) * mm});
            skLineSegment(sketch, "E28.6.8.0", {"start": v(-30.43, 9.89) * mm, "end": v(-30.14, 10.78) * mm});
            skLineSegment(sketch, "E28.9.8.0", {"start": v(-30.14, 10.78) * mm, "end": v(-28, 10.76) * mm});
            skLineSegment(sketch, "E28.2.9.0", {"start": v(-31.75, 4.08) * mm, "end": v(-29.84, 3.13) * mm});
            skLineSegment(sketch, "E28.3.9.0", {"start": v(-31.6, 5) * mm, "end": v(-31.75, 4.08) * mm});
            skLineSegment(sketch, "E28.6.9.0", {"start": v(-31.6, 5) * mm, "end": v(-31.46, 5.94) * mm});
            skLineSegment(sketch, "E28.9.9.0", {"start": v(-31.46, 5.94) * mm, "end": v(-29.34, 6.25) * mm});
            skLineSegment(sketch, "E28.2.10.0", {"start": v(-32, -0.94) * mm, "end": v(-29.96, -1.58) * mm});
            skLineSegment(sketch, "E28.3.10.0", {"start": v(-32, 0) * mm, "end": v(-32, -0.94) * mm});
            skLineSegment(sketch, "E28.6.10.0", {"start": v(-32, 0) * mm, "end": v(-32, 0.94) * mm});
            skLineSegment(sketch, "E28.9.10.0", {"start": v(-32, 0.94) * mm, "end": v(-29.96, 1.58) * mm});
            skLineSegment(sketch, "E28.2.11.0", {"start": v(-31.46, -5.94) * mm, "end": v(-29.34, -6.25) * mm});
            skLineSegment(sketch, "E28.3.11.0", {"start": v(-31.6, -5) * mm, "end": v(-31.46, -5.94) * mm});
            skLineSegment(sketch, "E28.6.11.0", {"start": v(-31.6, -5) * mm, "end": v(-31.75, -4.08) * mm});
            skLineSegment(sketch, "E28.9.11.0", {"start": v(-31.75, -4.08) * mm, "end": v(-29.84, -3.13) * mm});
            skLineSegment(sketch, "E28.2.12.0", {"start": v(-30.14, -10.78) * mm, "end": v(-28, -10.76) * mm});
            skLineSegment(sketch, "E28.3.12.0", {"start": v(-30.43, -9.89) * mm, "end": v(-30.14, -10.78) * mm});
            skLineSegment(sketch, "E28.6.12.0", {"start": v(-30.43, -9.89) * mm, "end": v(-30.73, -9) * mm});
            skLineSegment(sketch, "E28.9.12.0", {"start": v(-30.73, -9) * mm, "end": v(-28.98, -7.75) * mm});
            skLineSegment(sketch, "E28.2.13.0", {"start": v(-28.08, -15.37) * mm, "end": v(-25.98, -15) * mm});
            skLineSegment(sketch, "E28.3.13.0", {"start": v(-28.51, -14.53) * mm, "end": v(-28.08, -15.37) * mm});
            skLineSegment(sketch, "E28.6.13.0", {"start": v(-28.51, -14.53) * mm, "end": v(-28.94, -13.69) * mm});
            skLineSegment(sketch, "E28.9.13.0", {"start": v(-28.94, -13.69) * mm, "end": v(-27.41, -12.2) * mm});
            skLineSegment(sketch, "E28.2.14.0", {"start": v(-25.33, -19.57) * mm, "end": v(-23.3, -18.89) * mm});
            skLineSegment(sketch, "E28.3.14.0", {"start": v(-25.89, -18.8) * mm, "end": v(-25.33, -19.57) * mm});
            skLineSegment(sketch, "E28.6.14.0", {"start": v(-25.89, -18.8) * mm, "end": v(-26.44, -18.05) * mm});
            skLineSegment(sketch, "E28.9.14.0", {"start": v(-26.44, -18.05) * mm, "end": v(-25.17, -16.33) * mm});
            skLineSegment(sketch, "E28.2.15.0", {"start": v(-21.96, -23.3) * mm, "end": v(-20.07, -22.3) * mm});
            skLineSegment(sketch, "E28.3.15.0", {"start": v(-22.63, -22.63) * mm, "end": v(-21.96, -23.3) * mm});
            skLineSegment(sketch, "E28.6.15.0", {"start": v(-22.63, -22.63) * mm, "end": v(-23.3, -21.96) * mm});
            skLineSegment(sketch, "E28.9.15.0", {"start": v(-23.3, -21.96) * mm, "end": v(-22.3, -20.07) * mm});
            skLineSegment(sketch, "E28.2.16.0", {"start": v(-18.05, -26.44) * mm, "end": v(-16.33, -25.17) * mm});
            skLineSegment(sketch, "E28.3.16.0", {"start": v(-18.8, -25.89) * mm, "end": v(-18.05, -26.44) * mm});
            skLineSegment(sketch, "E28.6.16.0", {"start": v(-18.8, -25.89) * mm, "end": v(-19.57, -25.33) * mm});
            skLineSegment(sketch, "E28.9.16.0", {"start": v(-19.57, -25.33) * mm, "end": v(-18.89, -23.3) * mm});
            skLineSegment(sketch, "E28.2.17.0", {"start": v(-13.69, -28.94) * mm, "end": v(-12.2, -27.41) * mm});
            skLineSegment(sketch, "E28.3.17.0", {"start": v(-14.53, -28.51) * mm, "end": v(-13.69, -28.94) * mm});
            skLineSegment(sketch, "E28.6.17.0", {"start": v(-14.53, -28.51) * mm, "end": v(-15.37, -28.08) * mm});
            skLineSegment(sketch, "E28.9.17.0", {"start": v(-15.37, -28.08) * mm, "end": v(-15, -25.98) * mm});
            skLineSegment(sketch, "E28.2.18.0", {"start": v(-9, -30.73) * mm, "end": v(-7.75, -28.98) * mm});
            skLineSegment(sketch, "E28.3.18.0", {"start": v(-9.89, -30.43) * mm, "end": v(-9, -30.73) * mm});
            skLineSegment(sketch, "E28.6.18.0", {"start": v(-9.89, -30.43) * mm, "end": v(-10.78, -30.14) * mm});
            skLineSegment(sketch, "E28.9.18.0", {"start": v(-10.78, -30.14) * mm, "end": v(-10.76, -28) * mm});
            skLineSegment(sketch, "E28.2.19.0", {"start": v(-4.08, -31.75) * mm, "end": v(-3.13, -29.84) * mm});
            skLineSegment(sketch, "E28.3.19.0", {"start": v(-5, -31.6) * mm, "end": v(-4.08, -31.75) * mm});
            skLineSegment(sketch, "E28.6.19.0", {"start": v(-5, -31.6) * mm, "end": v(-5.94, -31.46) * mm});
            skLineSegment(sketch, "E28.9.19.0", {"start": v(-5.94, -31.46) * mm, "end": v(-6.25, -29.34) * mm});
            skLineSegment(sketch, "E28.2.20.0", {"start": v(0.94, -32) * mm, "end": v(1.58, -29.96) * mm});
            skLineSegment(sketch, "E28.3.20.0", {"start": v(0, -32) * mm, "end": v(0.94, -32) * mm});
            skLineSegment(sketch, "E28.6.20.0", {"start": v(0, -32) * mm, "end": v(-0.94, -32) * mm});
            skLineSegment(sketch, "E28.9.20.0", {"start": v(-0.94, -32) * mm, "end": v(-1.58, -29.96) * mm});
            skLineSegment(sketch, "E28.2.21.0", {"start": v(5.94, -31.46) * mm, "end": v(6.25, -29.34) * mm});
            skLineSegment(sketch, "E28.3.21.0", {"start": v(5, -31.6) * mm, "end": v(5.94, -31.46) * mm});
            skLineSegment(sketch, "E28.6.21.0", {"start": v(5, -31.6) * mm, "end": v(4.08, -31.75) * mm});
            skLineSegment(sketch, "E28.9.21.0", {"start": v(4.08, -31.75) * mm, "end": v(3.13, -29.84) * mm});
            skLineSegment(sketch, "E28.2.22.0", {"start": v(10.78, -30.14) * mm, "end": v(10.76, -28) * mm});
            skLineSegment(sketch, "E28.3.22.0", {"start": v(9.89, -30.43) * mm, "end": v(10.78, -30.14) * mm});
            skLineSegment(sketch, "E28.6.22.0", {"start": v(9.89, -30.43) * mm, "end": v(9, -30.73) * mm});
            skLineSegment(sketch, "E28.9.22.0", {"start": v(9, -30.73) * mm, "end": v(7.75, -28.98) * mm});
            skLineSegment(sketch, "E28.2.23.0", {"start": v(15.37, -28.08) * mm, "end": v(15, -25.98) * mm});
            skLineSegment(sketch, "E28.3.23.0", {"start": v(14.53, -28.51) * mm, "end": v(15.37, -28.08) * mm});
            skLineSegment(sketch, "E28.6.23.0", {"start": v(14.53, -28.51) * mm, "end": v(13.69, -28.94) * mm});
            skLineSegment(sketch, "E28.9.23.0", {"start": v(13.69, -28.94) * mm, "end": v(12.2, -27.41) * mm});
            skLineSegment(sketch, "E28.2.24.0", {"start": v(19.57, -25.33) * mm, "end": v(18.89, -23.3) * mm});
            skLineSegment(sketch, "E28.3.24.0", {"start": v(18.8, -25.89) * mm, "end": v(19.57, -25.33) * mm});
            skLineSegment(sketch, "E28.6.24.0", {"start": v(18.8, -25.89) * mm, "end": v(18.05, -26.44) * mm});
            skLineSegment(sketch, "E28.9.24.0", {"start": v(18.05, -26.44) * mm, "end": v(16.33, -25.17) * mm});
            skLineSegment(sketch, "E28.2.25.0", {"start": v(23.3, -21.96) * mm, "end": v(22.3, -20.07) * mm});
            skLineSegment(sketch, "E28.3.25.0", {"start": v(22.63, -22.63) * mm, "end": v(23.3, -21.96) * mm});
            skLineSegment(sketch, "E28.6.25.0", {"start": v(22.63, -22.63) * mm, "end": v(21.96, -23.3) * mm});
            skLineSegment(sketch, "E28.9.25.0", {"start": v(21.96, -23.3) * mm, "end": v(20.07, -22.3) * mm});
            skLineSegment(sketch, "E28.2.26.0", {"start": v(26.44, -18.05) * mm, "end": v(25.17, -16.33) * mm});
            skLineSegment(sketch, "E28.3.26.0", {"start": v(25.89, -18.8) * mm, "end": v(26.44, -18.05) * mm});
            skLineSegment(sketch, "E28.6.26.0", {"start": v(25.89, -18.8) * mm, "end": v(25.33, -19.57) * mm});
            skLineSegment(sketch, "E28.9.26.0", {"start": v(25.33, -19.57) * mm, "end": v(23.3, -18.89) * mm});
            skLineSegment(sketch, "E28.2.27.0", {"start": v(28.94, -13.69) * mm, "end": v(27.41, -12.2) * mm});
            skLineSegment(sketch, "E28.3.27.0", {"start": v(28.51, -14.53) * mm, "end": v(28.94, -13.69) * mm});
            skLineSegment(sketch, "E28.6.27.0", {"start": v(28.51, -14.53) * mm, "end": v(28.08, -15.37) * mm});
            skLineSegment(sketch, "E28.9.27.0", {"start": v(28.08, -15.37) * mm, "end": v(25.98, -15) * mm});
            skLineSegment(sketch, "E28.2.28.0", {"start": v(30.73, -9) * mm, "end": v(28.98, -7.75) * mm});
            skLineSegment(sketch, "E28.3.28.0", {"start": v(30.43, -9.89) * mm, "end": v(30.73, -9) * mm});
            skLineSegment(sketch, "E28.6.28.0", {"start": v(30.43, -9.89) * mm, "end": v(30.14, -10.78) * mm});
            skLineSegment(sketch, "E28.9.28.0", {"start": v(30.14, -10.78) * mm, "end": v(28, -10.76) * mm});
            skLineSegment(sketch, "E28.2.29.0", {"start": v(31.75, -4.08) * mm, "end": v(29.84, -3.13) * mm});
            skLineSegment(sketch, "E28.3.29.0", {"start": v(31.6, -5) * mm, "end": v(31.75, -4.08) * mm});
            skLineSegment(sketch, "E28.6.29.0", {"start": v(31.6, -5) * mm, "end": v(31.46, -5.94) * mm});
            skLineSegment(sketch, "E28.9.29.0", {"start": v(31.46, -5.94) * mm, "end": v(29.34, -6.25) * mm});
            skLineSegment(sketch, "E28.2.30.0", {"start": v(32, 0.94) * mm, "end": v(29.96, 1.58) * mm});
            skLineSegment(sketch, "E28.3.30.0", {"start": v(32, 0) * mm, "end": v(32, 0.94) * mm});
            skLineSegment(sketch, "E28.6.30.0", {"start": v(32, 0) * mm, "end": v(32, -0.94) * mm});
            skLineSegment(sketch, "E28.9.30.0", {"start": v(32, -0.94) * mm, "end": v(29.96, -1.58) * mm});
            skLineSegment(sketch, "E28.2.31.0", {"start": v(31.46, 5.94) * mm, "end": v(29.34, 6.25) * mm});
            skLineSegment(sketch, "E28.3.31.0", {"start": v(31.6, 5) * mm, "end": v(31.46, 5.94) * mm});
            skLineSegment(sketch, "E28.6.31.0", {"start": v(31.6, 5) * mm, "end": v(31.75, 4.08) * mm});
            skLineSegment(sketch, "E28.9.31.0", {"start": v(31.75, 4.08) * mm, "end": v(29.84, 3.13) * mm});
            skLineSegment(sketch, "E28.2.32.0", {"start": v(30.14, 10.78) * mm, "end": v(28, 10.76) * mm});
            skLineSegment(sketch, "E28.3.32.0", {"start": v(30.43, 9.89) * mm, "end": v(30.14, 10.78) * mm});
            skLineSegment(sketch, "E28.6.32.0", {"start": v(30.43, 9.89) * mm, "end": v(30.73, 9) * mm});
            skLineSegment(sketch, "E28.9.32.0", {"start": v(30.73, 9) * mm, "end": v(28.98, 7.75) * mm});
            skLineSegment(sketch, "E28.2.33.0", {"start": v(28.08, 15.37) * mm, "end": v(25.98, 15) * mm});
            skLineSegment(sketch, "E28.3.33.0", {"start": v(28.51, 14.53) * mm, "end": v(28.08, 15.37) * mm});
            skLineSegment(sketch, "E28.6.33.0", {"start": v(28.51, 14.53) * mm, "end": v(28.94, 13.69) * mm});
            skLineSegment(sketch, "E28.9.33.0", {"start": v(28.94, 13.69) * mm, "end": v(27.41, 12.2) * mm});
            skLineSegment(sketch, "E28.2.34.0", {"start": v(25.33, 19.57) * mm, "end": v(23.3, 18.89) * mm});
            skLineSegment(sketch, "E28.3.34.0", {"start": v(25.89, 18.8) * mm, "end": v(25.33, 19.57) * mm});
            skLineSegment(sketch, "E28.6.34.0", {"start": v(25.89, 18.8) * mm, "end": v(26.44, 18.05) * mm});
            skLineSegment(sketch, "E28.9.34.0", {"start": v(26.44, 18.05) * mm, "end": v(25.17, 16.33) * mm});
            skLineSegment(sketch, "E28.2.35.0", {"start": v(21.96, 23.3) * mm, "end": v(20.07, 22.3) * mm});
            skLineSegment(sketch, "E28.3.35.0", {"start": v(22.63, 22.63) * mm, "end": v(21.96, 23.3) * mm});
            skLineSegment(sketch, "E28.6.35.0", {"start": v(22.63, 22.63) * mm, "end": v(23.3, 21.96) * mm});
            skLineSegment(sketch, "E28.9.35.0", {"start": v(23.3, 21.96) * mm, "end": v(22.3, 20.07) * mm});
            skLineSegment(sketch, "E28.2.36.0", {"start": v(18.05, 26.44) * mm, "end": v(16.33, 25.17) * mm});
            skLineSegment(sketch, "E28.3.36.0", {"start": v(18.8, 25.89) * mm, "end": v(18.05, 26.44) * mm});
            skLineSegment(sketch, "E28.6.36.0", {"start": v(18.8, 25.89) * mm, "end": v(19.57, 25.33) * mm});
            skLineSegment(sketch, "E28.9.36.0", {"start": v(19.57, 25.33) * mm, "end": v(18.89, 23.3) * mm});
            skLineSegment(sketch, "E28.2.37.0", {"start": v(13.69, 28.94) * mm, "end": v(12.2, 27.41) * mm});
            skLineSegment(sketch, "E28.3.37.0", {"start": v(14.53, 28.51) * mm, "end": v(13.69, 28.94) * mm});
            skLineSegment(sketch, "E28.6.37.0", {"start": v(14.53, 28.51) * mm, "end": v(15.37, 28.08) * mm});
            skLineSegment(sketch, "E28.9.37.0", {"start": v(15.37, 28.08) * mm, "end": v(15, 25.98) * mm});
            skLineSegment(sketch, "E28.2.38.0", {"start": v(9, 30.73) * mm, "end": v(7.75, 28.98) * mm});
            skLineSegment(sketch, "E28.3.38.0", {"start": v(9.89, 30.43) * mm, "end": v(9, 30.73) * mm});
            skLineSegment(sketch, "E28.6.38.0", {"start": v(9.89, 30.43) * mm, "end": v(10.78, 30.14) * mm});
            skLineSegment(sketch, "E28.9.38.0", {"start": v(10.78, 30.14) * mm, "end": v(10.76, 28) * mm});
            skLineSegment(sketch, "E28.2.39.0", {"start": v(4.08, 31.75) * mm, "end": v(3.13, 29.84) * mm});
            skLineSegment(sketch, "E28.3.39.0", {"start": v(5, 31.6) * mm, "end": v(4.08, 31.75) * mm});
            skLineSegment(sketch, "E28.6.39.0", {"start": v(5, 31.6) * mm, "end": v(5.94, 31.46) * mm});
            skLineSegment(sketch, "E28.9.39.0", {"start": v(5.94, 31.46) * mm, "end": v(6.25, 29.34) * mm});
            skSolve(sketch);
        }
        {
            var Q0;
            Q0 = qSketchRegion(id + "F14", true);
            extrude(context, id + "F15", {"entities" : qUnion([Q0]), "operationType" : NewBodyOperationType.ADD, "depth" : 4 * mm, "offsetDistance" : 25 * mm});
        }
        {
            var Q0;
            Q0=makeQuery(id+"F7.opExtrude","CAP_FACE",FACE,{"disambiguationData":[OSD([sQuery(id+"F0.wireOp",EDGE,"E0")])],"isStart":false});
            var sketch = newSketch(context, id + "F16", { "sketchPlane" : qUnion([Q0])});
            skCircle(sketch, "E29", {"center": v(40, 0) * mm, "radius": 7.5 * mm});
            skLineSegment(sketch, "E30", {"start": v(40, 0) * mm, "end": v(40, 7.5) * mm, "construction": true});
            skLineSegment(sketch, "E31", {"start": v(40, 9.5) * mm, "end": v(39.06, 9.5) * mm});
            skLineSegment(sketch, "E32", {"start": v(39.06, 9.5) * mm, "end": v(38.68, 7.38) * mm});
            skLineSegment(sketch, "E33.MirrorCS", {"start": v(40, 9.5) * mm, "end": v(40.94, 9.5) * mm});
            skLineSegment(sketch, "E34.MirrorCS", {"start": v(40.94, 9.5) * mm, "end": v(41.32, 7.38) * mm});
            skLineSegment(sketch, "E35.1.0", {"start": v(34.42, 7.69) * mm, "end": v(33.65, 7.13) * mm});
            skLineSegment(sketch, "E35.1.1", {"start": v(33.65, 7.13) * mm, "end": v(34.6, 5.2) * mm});
            skLineSegment(sketch, "E35.1.2", {"start": v(34.42, 7.69) * mm, "end": v(35.18, 8.24) * mm});
            skLineSegment(sketch, "E35.1.3", {"start": v(35.18, 8.24) * mm, "end": v(36.72, 6.75) * mm});
            skLineSegment(sketch, "E35.2.0", {"start": v(30.96, 2.94) * mm, "end": v(30.67, 2.04) * mm});
            skLineSegment(sketch, "E35.2.1", {"start": v(30.67, 2.04) * mm, "end": v(32.57, 1.03) * mm});
            skLineSegment(sketch, "E35.2.2", {"start": v(30.96, 2.94) * mm, "end": v(31.26, 3.83) * mm});
            skLineSegment(sketch, "E35.2.3", {"start": v(31.26, 3.83) * mm, "end": v(33.38, 3.53) * mm});
            skLineSegment(sketch, "E36.2.3.0", {"start": v(30.96, -2.94) * mm, "end": v(31.26, -3.83) * mm});
            skLineSegment(sketch, "E36.3.3.0", {"start": v(31.26, -3.83) * mm, "end": v(33.38, -3.53) * mm});
            skLineSegment(sketch, "E36.6.3.0", {"start": v(30.96, -2.94) * mm, "end": v(30.67, -2.04) * mm});
            skLineSegment(sketch, "E36.9.3.0", {"start": v(30.67, -2.04) * mm, "end": v(32.57, -1.03) * mm});
            skLineSegment(sketch, "E36.2.4.0", {"start": v(34.42, -7.69) * mm, "end": v(35.18, -8.24) * mm});
            skLineSegment(sketch, "E36.3.4.0", {"start": v(35.18, -8.24) * mm, "end": v(36.72, -6.75) * mm});
            skLineSegment(sketch, "E36.6.4.0", {"start": v(34.42, -7.69) * mm, "end": v(33.65, -7.13) * mm});
            skLineSegment(sketch, "E36.9.4.0", {"start": v(33.65, -7.13) * mm, "end": v(34.6, -5.2) * mm});
            skLineSegment(sketch, "E36.2.5.0", {"start": v(40, -9.5) * mm, "end": v(40.94, -9.5) * mm});
            skLineSegment(sketch, "E36.3.5.0", {"start": v(40.94, -9.5) * mm, "end": v(41.32, -7.38) * mm});
            skLineSegment(sketch, "E36.6.5.0", {"start": v(40, -9.5) * mm, "end": v(39.06, -9.5) * mm});
            skLineSegment(sketch, "E36.9.5.0", {"start": v(39.06, -9.5) * mm, "end": v(38.68, -7.38) * mm});
            skLineSegment(sketch, "E36.2.6.0", {"start": v(45.58, -7.69) * mm, "end": v(46.35, -7.13) * mm});
            skLineSegment(sketch, "E36.3.6.0", {"start": v(46.35, -7.13) * mm, "end": v(45.4, -5.2) * mm});
            skLineSegment(sketch, "E36.6.6.0", {"start": v(45.58, -7.69) * mm, "end": v(44.82, -8.24) * mm});
            skLineSegment(sketch, "E36.9.6.0", {"start": v(44.82, -8.24) * mm, "end": v(43.28, -6.75) * mm});
            skLineSegment(sketch, "E36.2.7.0", {"start": v(49.04, -2.94) * mm, "end": v(49.33, -2.04) * mm});
            skLineSegment(sketch, "E36.3.7.0", {"start": v(49.33, -2.04) * mm, "end": v(47.43, -1.03) * mm});
            skLineSegment(sketch, "E36.6.7.0", {"start": v(49.04, -2.94) * mm, "end": v(48.74, -3.83) * mm});
            skLineSegment(sketch, "E36.9.7.0", {"start": v(48.74, -3.83) * mm, "end": v(46.62, -3.53) * mm});
            skLineSegment(sketch, "E36.2.8.0", {"start": v(49.04, 2.94) * mm, "end": v(48.74, 3.83) * mm});
            skLineSegment(sketch, "E36.3.8.0", {"start": v(48.74, 3.83) * mm, "end": v(46.62, 3.53) * mm});
            skLineSegment(sketch, "E36.6.8.0", {"start": v(49.04, 2.94) * mm, "end": v(49.33, 2.04) * mm});
            skLineSegment(sketch, "E36.9.8.0", {"start": v(49.33, 2.04) * mm, "end": v(47.43, 1.03) * mm});
            skLineSegment(sketch, "E36.2.9.0", {"start": v(45.58, 7.69) * mm, "end": v(44.82, 8.24) * mm});
            skLineSegment(sketch, "E36.3.9.0", {"start": v(44.82, 8.24) * mm, "end": v(43.28, 6.75) * mm});
            skLineSegment(sketch, "E36.6.9.0", {"start": v(45.58, 7.69) * mm, "end": v(46.35, 7.13) * mm});
            skLineSegment(sketch, "E36.9.9.0", {"start": v(46.35, 7.13) * mm, "end": v(45.4, 5.2) * mm});
            skSolve(sketch);
        }
        {
            var Q0;
            Q0 = qSketchRegion(id + "F16", true);
            extrude(context, id + "F17", {"entities" : qUnion([Q0]), "operationType" : NewBodyOperationType.ADD, "depth" : 4 * mm, "offsetDistance" : 25 * mm});
        }
        {
            var Q0;
            Q0=makeQuery(id+"F17.opExtrude","CAP_FACE",FACE,{"disambiguationData":[OSD([sQuery(id+"F16.wireOp",EDGE,"E29"),sQuery(id+"F16.wireOp",EDGE,"E31"),sQuery(id+"F16.wireOp",EDGE,"E32"),sQuery(id+"F16.wireOp",EDGE,"E33.MirrorCS"),sQuery(id+"F16.wireOp",EDGE,"E34.MirrorCS"),sQuery(id+"F16.wireOp",EDGE,"E35.1.0"),sQuery(id+"F16.wireOp",EDGE,"E35.1.1"),sQuery(id+"F16.wireOp",EDGE,"E35.1.2"),sQuery(id+"F16.wireOp",EDGE,"E35.1.3"),sQuery(id+"F16.wireOp",EDGE,"E35.2.0"),sQuery(id+"F16.wireOp",EDGE,"E35.2.1"),sQuery(id+"F16.wireOp",EDGE,"E35.2.2"),sQuery(id+"F16.wireOp",EDGE,"E35.2.3"),sQuery(id+"F16.wireOp",EDGE,"E36.2.3.0"),sQuery(id+"F16.wireOp",EDGE,"E36.3.3.0"),sQuery(id+"F16.wireOp",EDGE,"E36.6.3.0"),sQuery(id+"F16.wireOp",EDGE,"E36.9.3.0"),sQuery(id+"F16.wireOp",EDGE,"E36.2.4.0"),sQuery(id+"F16.wireOp",EDGE,"E36.3.4.0"),sQuery(id+"F16.wireOp",EDGE,"E36.6.4.0"),sQuery(id+"F16.wireOp",EDGE,"E36.9.4.0"),sQuery(id+"F16.wireOp",EDGE,"E36.2.5.0"),sQuery(id+"F16.wireOp",EDGE,"E36.3.5.0"),sQuery(id+"F16.wireOp",EDGE,"E36.6.5.0"),sQuery(id+"F16.wireOp",EDGE,"E36.9.5.0"),sQuery(id+"F16.wireOp",EDGE,"E36.2.6.0"),sQuery(id+"F16.wireOp",EDGE,"E36.3.6.0"),sQuery(id+"F16.wireOp",EDGE,"E36.6.6.0"),sQuery(id+"F16.wireOp",EDGE,"E36.9.6.0"),sQuery(id+"F16.wireOp",EDGE,"E36.2.7.0"),sQuery(id+"F16.wireOp",EDGE,"E36.3.7.0"),sQuery(id+"F16.wireOp",EDGE,"E36.6.7.0"),sQuery(id+"F16.wireOp",EDGE,"E36.9.7.0"),sQuery(id+"F16.wireOp",EDGE,"E36.2.8.0"),sQuery(id+"F16.wireOp",EDGE,"E36.3.8.0"),sQuery(id+"F16.wireOp",EDGE,"E36.6.8.0"),sQuery(id+"F16.wireOp",EDGE,"E36.9.8.0"),sQuery(id+"F16.wireOp",EDGE,"E36.2.9.0"),sQuery(id+"F16.wireOp",EDGE,"E36.3.9.0"),sQuery(id+"F16.wireOp",EDGE,"E36.6.9.0"),sQuery(id+"F16.wireOp",EDGE,"E36.9.9.0")])],"isStart":false});
            var sketch = newSketch(context, id + "F18", { "sketchPlane" : qUnion([Q0])});
            skCircle(sketch, "E37.0", {"center": v(40, 0) * mm, "radius": 3 * mm});
            skSolve(sketch);
        }
        {
            var Q0;
            Q0 = qSketchRegion(id + "F18", true);
            extrude(context, id + "F19", {"entities" : qUnion([Q0]), "operationType" : NewBodyOperationType.ADD, "depth" : 2 * mm, "offsetDistance" : 25 * mm});
        }
        {
            var Q0;
            Q0=makeQuery(id+"F19.opExtrude","CAP_FACE",FACE,{"disambiguationData":[OSD([sQuery(id+"F18.wireOp",EDGE,"E37.0")])],"isStart":false});
            var sketch = newSketch(context, id + "F20", { "sketchPlane" : qUnion([Q0])});
            skCircle(sketch, "E38", {"center": v(0, 0) * mm, "radius": 98 * mm});
            skCircle(sketch, "E39.0", {"center": v(0, 0) * mm, "radius": 5 * mm});
            skSolve(sketch);
        }
        {
            var Q0;
            Q0 = qSketchRegion(id + "F20", true);
            extrude(context, id + "F21", {"entities" : qUnion([Q0]), "depth" : 1 * mm, "offsetDistance" : 25 * mm});
        }
        {
            var Q0;
            Q0=makeQuery(id+"F21.opExtrude","SWEPT_BODY",BODY,{"disambiguationData":[OSD([sQuery(id+"F20.wireOp",EDGE,"E38"),sQuery(id+"F20.wireOp",EDGE,"E39.0")])]});
            var Q1;
            Q1=makeQuery(id+"F1.opExtrude","SWEPT_BODY",BODY,{"disambiguationData":[OSD([sQuery(id+"F0.wireOp",EDGE,"E0")])]});
            booleanBodies(context, id + "F22", {"operationType" : BooleanOperationType.SUBTRACTION, "tools" : qUnion([Q0]), "targets" : qUnion([Q1]), "keepTools" : true});
        }
        {
            var Q0;
            Q0=makeQuery(id+"F21.opExtrude","CAP_FACE",FACE,{"disambiguationData":[OSD([sQuery(id+"F20.wireOp",EDGE,"E38"),sQuery(id+"F20.wireOp",EDGE,"E39.0")])],"isStart":true});
            var sketch = newSketch(context, id + "F23", { "sketchPlane" : qUnion([Q0])});
            skCircle(sketch, "E40.0.0", {"center": v(-40, 0) * mm, "radius": 3 * mm});
            skCircle(sketch, "E41", {"center": v(-40, 0) * mm, "radius": 5 * mm});
            skSolve(sketch);
        }
        {
            var Q0;
            Q0 = qSketchRegion(id + "F23", true);
            extrude(context, id + "F24", {"entities" : qUnion([Q0]), "operationType" : NewBodyOperationType.ADD, "endBound" : BoundingType.UP_TO_NEXT, "depth" : 25 * mm, "offsetDistance" : 25 * mm});
        }
        {
            var Q0;
            Q0=makeQuery(id+"F21.opExtrude","CAP_FACE",FACE,{"disambiguationData":[OSD([sQuery(id+"F20.wireOp",EDGE,"E38"),sQuery(id+"F20.wireOp",EDGE,"E39.0")])],"isStart":false});
            var sketch = newSketch(context, id + "F25", { "sketchPlane" : qUnion([Q0])});
            skLineSegment(sketch, "E42.bottom", {"start": v(-1.5, 71) * mm, "end": v(1.5, 71) * mm});
            skLineSegment(sketch, "E42.top", {"start": v(-1.5, 91) * mm, "end": v(1.5, 91) * mm});
            skLineSegment(sketch, "E42.left", {"start": v(-1.5, 71) * mm, "end": v(-1.5, 91) * mm});
            skLineSegment(sketch, "E42.right", {"start": v(1.5, 71) * mm, "end": v(1.5, 91) * mm});
            skPoint(sketch, "E42.middle", {"position": v(0, 81) * mm});
            skLineSegment(sketch, "E43.1.0", {"start": v(-36.8, 60.74) * mm, "end": v(-46.8, 78.06) * mm});
            skLineSegment(sketch, "E43.1.1", {"start": v(-46.8, 78.06) * mm, "end": v(-44.2, 79.56) * mm});
            skLineSegment(sketch, "E43.1.2", {"start": v(-34.2, 62.24) * mm, "end": v(-44.2, 79.56) * mm});
            skLineSegment(sketch, "E43.1.3", {"start": v(-36.8, 60.74) * mm, "end": v(-34.2, 62.24) * mm});
            skLineSegment(sketch, "E43.2.0", {"start": v(-62.24, 34.2) * mm, "end": v(-79.56, 44.2) * mm});
            skLineSegment(sketch, "E43.2.1", {"start": v(-79.56, 44.2) * mm, "end": v(-78.06, 46.8) * mm});
            skLineSegment(sketch, "E43.2.2", {"start": v(-60.74, 36.8) * mm, "end": v(-78.06, 46.8) * mm});
            skLineSegment(sketch, "E43.2.3", {"start": v(-62.24, 34.2) * mm, "end": v(-60.74, 36.8) * mm});
            skPoint(sketch, "E43.center", {"position": v(0, 0) * mm});
            skLineSegment(sketch, "E44.1.3.0", {"start": v(-71, -1.5) * mm, "end": v(-91, -1.5) * mm});
            skLineSegment(sketch, "E44.3.3.0", {"start": v(-91, -1.5) * mm, "end": v(-91, 1.5) * mm});
            skLineSegment(sketch, "E44.6.3.0", {"start": v(-71, 1.5) * mm, "end": v(-91, 1.5) * mm});
            skLineSegment(sketch, "E44.9.3.0", {"start": v(-71, -1.5) * mm, "end": v(-71, 1.5) * mm});
            skLineSegment(sketch, "E44.1.4.0", {"start": v(-60.74, -36.8) * mm, "end": v(-78.06, -46.8) * mm});
            skLineSegment(sketch, "E44.3.4.0", {"start": v(-78.06, -46.8) * mm, "end": v(-79.56, -44.2) * mm});
            skLineSegment(sketch, "E44.6.4.0", {"start": v(-62.24, -34.2) * mm, "end": v(-79.56, -44.2) * mm});
            skLineSegment(sketch, "E44.9.4.0", {"start": v(-60.74, -36.8) * mm, "end": v(-62.24, -34.2) * mm});
            skLineSegment(sketch, "E44.1.5.0", {"start": v(-34.2, -62.24) * mm, "end": v(-44.2, -79.56) * mm});
            skLineSegment(sketch, "E44.3.5.0", {"start": v(-44.2, -79.56) * mm, "end": v(-46.8, -78.06) * mm});
            skLineSegment(sketch, "E44.6.5.0", {"start": v(-36.8, -60.74) * mm, "end": v(-46.8, -78.06) * mm});
            skLineSegment(sketch, "E44.9.5.0", {"start": v(-34.2, -62.24) * mm, "end": v(-36.8, -60.74) * mm});
            skLineSegment(sketch, "E44.1.6.0", {"start": v(1.5, -71) * mm, "end": v(1.5, -91) * mm});
            skLineSegment(sketch, "E44.3.6.0", {"start": v(1.5, -91) * mm, "end": v(-1.5, -91) * mm});
            skLineSegment(sketch, "E44.6.6.0", {"start": v(-1.5, -71) * mm, "end": v(-1.5, -91) * mm});
            skLineSegment(sketch, "E44.9.6.0", {"start": v(1.5, -71) * mm, "end": v(-1.5, -71) * mm});
            skLineSegment(sketch, "E44.1.7.0", {"start": v(36.8, -60.74) * mm, "end": v(46.8, -78.06) * mm});
            skLineSegment(sketch, "E44.3.7.0", {"start": v(46.8, -78.06) * mm, "end": v(44.2, -79.56) * mm});
            skLineSegment(sketch, "E44.6.7.0", {"start": v(34.2, -62.24) * mm, "end": v(44.2, -79.56) * mm});
            skLineSegment(sketch, "E44.9.7.0", {"start": v(36.8, -60.74) * mm, "end": v(34.2, -62.24) * mm});
            skLineSegment(sketch, "E44.1.8.0", {"start": v(62.24, -34.2) * mm, "end": v(79.56, -44.2) * mm});
            skLineSegment(sketch, "E44.3.8.0", {"start": v(79.56, -44.2) * mm, "end": v(78.06, -46.8) * mm});
            skLineSegment(sketch, "E44.6.8.0", {"start": v(60.74, -36.8) * mm, "end": v(78.06, -46.8) * mm});
            skLineSegment(sketch, "E44.9.8.0", {"start": v(62.24, -34.2) * mm, "end": v(60.74, -36.8) * mm});
            skLineSegment(sketch, "E44.1.9.0", {"start": v(71, 1.5) * mm, "end": v(91, 1.5) * mm});
            skLineSegment(sketch, "E44.3.9.0", {"start": v(91, 1.5) * mm, "end": v(91, -1.5) * mm});
            skLineSegment(sketch, "E44.6.9.0", {"start": v(71, -1.5) * mm, "end": v(91, -1.5) * mm});
            skLineSegment(sketch, "E44.9.9.0", {"start": v(71, 1.5) * mm, "end": v(71, -1.5) * mm});
            skLineSegment(sketch, "E44.1.10.0", {"start": v(60.74, 36.8) * mm, "end": v(78.06, 46.8) * mm});
            skLineSegment(sketch, "E44.3.10.0", {"start": v(78.06, 46.8) * mm, "end": v(79.56, 44.2) * mm});
            skLineSegment(sketch, "E44.6.10.0", {"start": v(62.24, 34.2) * mm, "end": v(79.56, 44.2) * mm});
            skLineSegment(sketch, "E44.9.10.0", {"start": v(60.74, 36.8) * mm, "end": v(62.24, 34.2) * mm});
            skLineSegment(sketch, "E44.1.11.0", {"start": v(34.2, 62.24) * mm, "end": v(44.2, 79.56) * mm});
            skLineSegment(sketch, "E44.3.11.0", {"start": v(44.2, 79.56) * mm, "end": v(46.8, 78.06) * mm});
            skLineSegment(sketch, "E44.6.11.0", {"start": v(36.8, 60.74) * mm, "end": v(46.8, 78.06) * mm});
            skLineSegment(sketch, "E44.9.11.0", {"start": v(34.2, 62.24) * mm, "end": v(36.8, 60.74) * mm});
            skSolve(sketch);
        }
        {
            var Q0;
            Q0 = qSketchRegion(id + "F25", true);
            extrude(context, id + "F26", {"entities" : qUnion([Q0]), "operationType" : NewBodyOperationType.REMOVE, "oppositeDirection" : true, "depth" : 0.5 * mm, "offsetDistance" : 25 * mm});
        }
        {
            var Q0;
            Q0=makeQuery(id+"F21.opExtrude","CAP_FACE",FACE,{"disambiguationData":[OSD([sQuery(id+"F20.wireOp",EDGE,"E38"),sQuery(id+"F20.wireOp",EDGE,"E39.0")])],"isStart":false});
            var sketch = newSketch(context, id + "F27", { "sketchPlane" : qUnion([Q0])});
            skLineSegment(sketch, "E45.bottom", {"start": v(-0.75, 78.5) * mm, "end": v(0.75, 78.5) * mm});
            skLineSegment(sketch, "E45.top", {"start": v(-0.75, 90.5) * mm, "end": v(0.75, 90.5) * mm});
            skLineSegment(sketch, "E45.left", {"start": v(-0.75, 78.5) * mm, "end": v(-0.75, 90.5) * mm});
            skLineSegment(sketch, "E45.right", {"start": v(0.75, 78.5) * mm, "end": v(0.75, 90.5) * mm});
            skPoint(sketch, "E45.middle", {"position": v(0, 84.5) * mm});
            skLineSegment(sketch, "E46.1.0", {"start": v(-8.95, 78) * mm, "end": v(-10.2, 89.93) * mm});
            skLineSegment(sketch, "E46.1.1", {"start": v(-10.2, 89.93) * mm, "end": v(-8.71, 90.08) * mm});
            skLineSegment(sketch, "E46.1.2", {"start": v(-7.46, 78.15) * mm, "end": v(-8.71, 90.08) * mm});
            skLineSegment(sketch, "E46.1.3", {"start": v(-8.95, 78) * mm, "end": v(-7.46, 78.15) * mm});
            skLineSegment(sketch, "E46.2.0", {"start": v(-17.05, 76.63) * mm, "end": v(-19.55, 88.37) * mm});
            skLineSegment(sketch, "E46.2.1", {"start": v(-19.55, 88.37) * mm, "end": v(-18.08, 88.68) * mm});
            skLineSegment(sketch, "E46.2.2", {"start": v(-15.59, 76.94) * mm, "end": v(-18.08, 88.68) * mm});
            skLineSegment(sketch, "E46.2.3", {"start": v(-17.05, 76.63) * mm, "end": v(-15.59, 76.94) * mm});
            skPoint(sketch, "E46.center", {"position": v(0, 0) * mm});
            skLineSegment(sketch, "E47.1.3.0", {"start": v(-24.97, 74.43) * mm, "end": v(-28.68, 85.84) * mm});
            skLineSegment(sketch, "E47.3.3.0", {"start": v(-28.68, 85.84) * mm, "end": v(-27.25, 86.3) * mm});
            skLineSegment(sketch, "E47.6.3.0", {"start": v(-23.54, 74.89) * mm, "end": v(-27.25, 86.3) * mm});
            skLineSegment(sketch, "E47.9.3.0", {"start": v(-24.97, 74.43) * mm, "end": v(-23.54, 74.89) * mm});
            skLineSegment(sketch, "E47.1.4.0", {"start": v(-32.61, 71.4) * mm, "end": v(-37.5, 82.37) * mm});
            skLineSegment(sketch, "E47.3.4.0", {"start": v(-37.5, 82.37) * mm, "end": v(-36.12, 82.98) * mm});
            skLineSegment(sketch, "E47.6.4.0", {"start": v(-31.24, 72.02) * mm, "end": v(-36.12, 82.98) * mm});
            skLineSegment(sketch, "E47.9.4.0", {"start": v(-32.61, 71.4) * mm, "end": v(-31.24, 72.02) * mm});
            skLineSegment(sketch, "E47.1.5.0", {"start": v(-39.9, 67.6) * mm, "end": v(-45.9, 78) * mm});
            skLineSegment(sketch, "E47.3.5.0", {"start": v(-45.9, 78) * mm, "end": v(-44.6, 78.75) * mm});
            skLineSegment(sketch, "E47.6.5.0", {"start": v(-38.6, 68.36) * mm, "end": v(-44.6, 78.75) * mm});
            skLineSegment(sketch, "E47.9.5.0", {"start": v(-39.9, 67.6) * mm, "end": v(-38.6, 68.36) * mm});
            skLineSegment(sketch, "E47.1.6.0", {"start": v(-46.75, 63.07) * mm, "end": v(-53.8, 72.78) * mm});
            skLineSegment(sketch, "E47.3.6.0", {"start": v(-53.8, 72.78) * mm, "end": v(-52.59, 73.66) * mm});
            skLineSegment(sketch, "E47.6.6.0", {"start": v(-45.53, 63.95) * mm, "end": v(-52.59, 73.66) * mm});
            skLineSegment(sketch, "E47.9.6.0", {"start": v(-46.75, 63.07) * mm, "end": v(-45.53, 63.95) * mm});
            skLineSegment(sketch, "E47.1.7.0", {"start": v(-53.08, 57.84) * mm, "end": v(-61.11, 66.75) * mm});
            skLineSegment(sketch, "E47.3.7.0", {"start": v(-61.11, 66.75) * mm, "end": v(-60, 67.76) * mm});
            skLineSegment(sketch, "E47.6.7.0", {"start": v(-51.97, 58.84) * mm, "end": v(-60, 67.76) * mm});
            skLineSegment(sketch, "E47.9.7.0", {"start": v(-53.08, 57.84) * mm, "end": v(-51.97, 58.84) * mm});
            skLineSegment(sketch, "E47.1.8.0", {"start": v(-58.84, 51.97) * mm, "end": v(-67.76, 60) * mm});
            skLineSegment(sketch, "E47.3.8.0", {"start": v(-67.76, 60) * mm, "end": v(-66.75, 61.11) * mm});
            skLineSegment(sketch, "E47.6.8.0", {"start": v(-57.84, 53.08) * mm, "end": v(-66.75, 61.11) * mm});
            skLineSegment(sketch, "E47.9.8.0", {"start": v(-58.84, 51.97) * mm, "end": v(-57.84, 53.08) * mm});
            skLineSegment(sketch, "E47.1.9.0", {"start": v(-63.95, 45.53) * mm, "end": v(-73.66, 52.59) * mm});
            skLineSegment(sketch, "E47.3.9.0", {"start": v(-73.66, 52.59) * mm, "end": v(-72.78, 53.8) * mm});
            skLineSegment(sketch, "E47.6.9.0", {"start": v(-63.07, 46.75) * mm, "end": v(-72.78, 53.8) * mm});
            skLineSegment(sketch, "E47.9.9.0", {"start": v(-63.95, 45.53) * mm, "end": v(-63.07, 46.75) * mm});
            skLineSegment(sketch, "E47.1.10.0", {"start": v(-68.36, 38.6) * mm, "end": v(-78.75, 44.6) * mm});
            skLineSegment(sketch, "E47.3.10.0", {"start": v(-78.75, 44.6) * mm, "end": v(-78, 45.9) * mm});
            skLineSegment(sketch, "E47.6.10.0", {"start": v(-67.6, 39.9) * mm, "end": v(-78, 45.9) * mm});
            skLineSegment(sketch, "E47.9.10.0", {"start": v(-68.36, 38.6) * mm, "end": v(-67.6, 39.9) * mm});
            skLineSegment(sketch, "E47.1.11.0", {"start": v(-72.02, 31.24) * mm, "end": v(-82.98, 36.12) * mm});
            skLineSegment(sketch, "E47.3.11.0", {"start": v(-82.98, 36.12) * mm, "end": v(-82.37, 37.5) * mm});
            skLineSegment(sketch, "E47.6.11.0", {"start": v(-71.4, 32.61) * mm, "end": v(-82.37, 37.5) * mm});
            skLineSegment(sketch, "E47.9.11.0", {"start": v(-72.02, 31.24) * mm, "end": v(-71.4, 32.61) * mm});
            skLineSegment(sketch, "E47.1.12.0", {"start": v(-74.89, 23.54) * mm, "end": v(-86.3, 27.25) * mm});
            skLineSegment(sketch, "E47.3.12.0", {"start": v(-86.3, 27.25) * mm, "end": v(-85.84, 28.68) * mm});
            skLineSegment(sketch, "E47.6.12.0", {"start": v(-74.43, 24.97) * mm, "end": v(-85.84, 28.68) * mm});
            skLineSegment(sketch, "E47.9.12.0", {"start": v(-74.89, 23.54) * mm, "end": v(-74.43, 24.97) * mm});
            skLineSegment(sketch, "E47.1.13.0", {"start": v(-76.94, 15.59) * mm, "end": v(-88.68, 18.08) * mm});
            skLineSegment(sketch, "E47.3.13.0", {"start": v(-88.68, 18.08) * mm, "end": v(-88.37, 19.55) * mm});
            skLineSegment(sketch, "E47.6.13.0", {"start": v(-76.63, 17.05) * mm, "end": v(-88.37, 19.55) * mm});
            skLineSegment(sketch, "E47.9.13.0", {"start": v(-76.94, 15.59) * mm, "end": v(-76.63, 17.05) * mm});
            skLineSegment(sketch, "E47.1.14.0", {"start": v(-78.15, 7.46) * mm, "end": v(-90.08, 8.71) * mm});
            skLineSegment(sketch, "E47.3.14.0", {"start": v(-90.08, 8.71) * mm, "end": v(-89.93, 10.2) * mm});
            skLineSegment(sketch, "E47.6.14.0", {"start": v(-78, 8.95) * mm, "end": v(-89.93, 10.2) * mm});
            skLineSegment(sketch, "E47.9.14.0", {"start": v(-78.15, 7.46) * mm, "end": v(-78, 8.95) * mm});
            skLineSegment(sketch, "E47.1.15.0", {"start": v(-78.5, -0.75) * mm, "end": v(-90.5, -0.75) * mm});
            skLineSegment(sketch, "E47.3.15.0", {"start": v(-90.5, -0.75) * mm, "end": v(-90.5, 0.75) * mm});
            skLineSegment(sketch, "E47.6.15.0", {"start": v(-78.5, 0.75) * mm, "end": v(-90.5, 0.75) * mm});
            skLineSegment(sketch, "E47.9.15.0", {"start": v(-78.5, -0.75) * mm, "end": v(-78.5, 0.75) * mm});
            skLineSegment(sketch, "E47.1.16.0", {"start": v(-78, -8.95) * mm, "end": v(-89.93, -10.2) * mm});
            skLineSegment(sketch, "E47.3.16.0", {"start": v(-89.93, -10.2) * mm, "end": v(-90.08, -8.71) * mm});
            skLineSegment(sketch, "E47.6.16.0", {"start": v(-78.15, -7.46) * mm, "end": v(-90.08, -8.71) * mm});
            skLineSegment(sketch, "E47.9.16.0", {"start": v(-78, -8.95) * mm, "end": v(-78.15, -7.46) * mm});
            skLineSegment(sketch, "E47.1.17.0", {"start": v(-76.63, -17.05) * mm, "end": v(-88.37, -19.55) * mm});
            skLineSegment(sketch, "E47.3.17.0", {"start": v(-88.37, -19.55) * mm, "end": v(-88.68, -18.08) * mm});
            skLineSegment(sketch, "E47.6.17.0", {"start": v(-76.94, -15.59) * mm, "end": v(-88.68, -18.08) * mm});
            skLineSegment(sketch, "E47.9.17.0", {"start": v(-76.63, -17.05) * mm, "end": v(-76.94, -15.59) * mm});
            skLineSegment(sketch, "E47.1.18.0", {"start": v(-74.43, -24.97) * mm, "end": v(-85.84, -28.68) * mm});
            skLineSegment(sketch, "E47.3.18.0", {"start": v(-85.84, -28.68) * mm, "end": v(-86.3, -27.25) * mm});
            skLineSegment(sketch, "E47.6.18.0", {"start": v(-74.89, -23.54) * mm, "end": v(-86.3, -27.25) * mm});
            skLineSegment(sketch, "E47.9.18.0", {"start": v(-74.43, -24.97) * mm, "end": v(-74.89, -23.54) * mm});
            skLineSegment(sketch, "E47.1.19.0", {"start": v(-71.4, -32.61) * mm, "end": v(-82.37, -37.5) * mm});
            skLineSegment(sketch, "E47.3.19.0", {"start": v(-82.37, -37.5) * mm, "end": v(-82.98, -36.12) * mm});
            skLineSegment(sketch, "E47.6.19.0", {"start": v(-72.02, -31.24) * mm, "end": v(-82.98, -36.12) * mm});
            skLineSegment(sketch, "E47.9.19.0", {"start": v(-71.4, -32.61) * mm, "end": v(-72.02, -31.24) * mm});
            skLineSegment(sketch, "E47.1.20.0", {"start": v(-67.6, -39.9) * mm, "end": v(-78, -45.9) * mm});
            skLineSegment(sketch, "E47.3.20.0", {"start": v(-78, -45.9) * mm, "end": v(-78.75, -44.6) * mm});
            skLineSegment(sketch, "E47.6.20.0", {"start": v(-68.36, -38.6) * mm, "end": v(-78.75, -44.6) * mm});
            skLineSegment(sketch, "E47.9.20.0", {"start": v(-67.6, -39.9) * mm, "end": v(-68.36, -38.6) * mm});
            skLineSegment(sketch, "E47.1.21.0", {"start": v(-63.07, -46.75) * mm, "end": v(-72.78, -53.8) * mm});
            skLineSegment(sketch, "E47.3.21.0", {"start": v(-72.78, -53.8) * mm, "end": v(-73.66, -52.59) * mm});
            skLineSegment(sketch, "E47.6.21.0", {"start": v(-63.95, -45.53) * mm, "end": v(-73.66, -52.59) * mm});
            skLineSegment(sketch, "E47.9.21.0", {"start": v(-63.07, -46.75) * mm, "end": v(-63.95, -45.53) * mm});
            skLineSegment(sketch, "E47.1.22.0", {"start": v(-57.84, -53.08) * mm, "end": v(-66.75, -61.11) * mm});
            skLineSegment(sketch, "E47.3.22.0", {"start": v(-66.75, -61.11) * mm, "end": v(-67.76, -60) * mm});
            skLineSegment(sketch, "E47.6.22.0", {"start": v(-58.84, -51.97) * mm, "end": v(-67.76, -60) * mm});
            skLineSegment(sketch, "E47.9.22.0", {"start": v(-57.84, -53.08) * mm, "end": v(-58.84, -51.97) * mm});
            skLineSegment(sketch, "E47.1.23.0", {"start": v(-51.97, -58.84) * mm, "end": v(-60, -67.76) * mm});
            skLineSegment(sketch, "E47.3.23.0", {"start": v(-60, -67.76) * mm, "end": v(-61.11, -66.75) * mm});
            skLineSegment(sketch, "E47.6.23.0", {"start": v(-53.08, -57.84) * mm, "end": v(-61.11, -66.75) * mm});
            skLineSegment(sketch, "E47.9.23.0", {"start": v(-51.97, -58.84) * mm, "end": v(-53.08, -57.84) * mm});
            skLineSegment(sketch, "E47.1.24.0", {"start": v(-45.53, -63.95) * mm, "end": v(-52.59, -73.66) * mm});
            skLineSegment(sketch, "E47.3.24.0", {"start": v(-52.59, -73.66) * mm, "end": v(-53.8, -72.78) * mm});
            skLineSegment(sketch, "E47.6.24.0", {"start": v(-46.75, -63.07) * mm, "end": v(-53.8, -72.78) * mm});
            skLineSegment(sketch, "E47.9.24.0", {"start": v(-45.53, -63.95) * mm, "end": v(-46.75, -63.07) * mm});
            skLineSegment(sketch, "E47.1.25.0", {"start": v(-38.6, -68.36) * mm, "end": v(-44.6, -78.75) * mm});
            skLineSegment(sketch, "E47.3.25.0", {"start": v(-44.6, -78.75) * mm, "end": v(-45.9, -78) * mm});
            skLineSegment(sketch, "E47.6.25.0", {"start": v(-39.9, -67.6) * mm, "end": v(-45.9, -78) * mm});
            skLineSegment(sketch, "E47.9.25.0", {"start": v(-38.6, -68.36) * mm, "end": v(-39.9, -67.6) * mm});
            skLineSegment(sketch, "E47.1.26.0", {"start": v(-31.24, -72.02) * mm, "end": v(-36.12, -82.98) * mm});
            skLineSegment(sketch, "E47.3.26.0", {"start": v(-36.12, -82.98) * mm, "end": v(-37.5, -82.37) * mm});
            skLineSegment(sketch, "E47.6.26.0", {"start": v(-32.61, -71.4) * mm, "end": v(-37.5, -82.37) * mm});
            skLineSegment(sketch, "E47.9.26.0", {"start": v(-31.24, -72.02) * mm, "end": v(-32.61, -71.4) * mm});
            skLineSegment(sketch, "E47.1.27.0", {"start": v(-23.54, -74.89) * mm, "end": v(-27.25, -86.3) * mm});
            skLineSegment(sketch, "E47.3.27.0", {"start": v(-27.25, -86.3) * mm, "end": v(-28.68, -85.84) * mm});
            skLineSegment(sketch, "E47.6.27.0", {"start": v(-24.97, -74.43) * mm, "end": v(-28.68, -85.84) * mm});
            skLineSegment(sketch, "E47.9.27.0", {"start": v(-23.54, -74.89) * mm, "end": v(-24.97, -74.43) * mm});
            skLineSegment(sketch, "E47.1.28.0", {"start": v(-15.59, -76.94) * mm, "end": v(-18.08, -88.68) * mm});
            skLineSegment(sketch, "E47.3.28.0", {"start": v(-18.08, -88.68) * mm, "end": v(-19.55, -88.37) * mm});
            skLineSegment(sketch, "E47.6.28.0", {"start": v(-17.05, -76.63) * mm, "end": v(-19.55, -88.37) * mm});
            skLineSegment(sketch, "E47.9.28.0", {"start": v(-15.59, -76.94) * mm, "end": v(-17.05, -76.63) * mm});
            skLineSegment(sketch, "E47.1.29.0", {"start": v(-7.46, -78.15) * mm, "end": v(-8.71, -90.08) * mm});
            skLineSegment(sketch, "E47.3.29.0", {"start": v(-8.71, -90.08) * mm, "end": v(-10.2, -89.93) * mm});
            skLineSegment(sketch, "E47.6.29.0", {"start": v(-8.95, -78) * mm, "end": v(-10.2, -89.93) * mm});
            skLineSegment(sketch, "E47.9.29.0", {"start": v(-7.46, -78.15) * mm, "end": v(-8.95, -78) * mm});
            skLineSegment(sketch, "E47.1.30.0", {"start": v(0.75, -78.5) * mm, "end": v(0.75, -90.5) * mm});
            skLineSegment(sketch, "E47.3.30.0", {"start": v(0.75, -90.5) * mm, "end": v(-0.75, -90.5) * mm});
            skLineSegment(sketch, "E47.6.30.0", {"start": v(-0.75, -78.5) * mm, "end": v(-0.75, -90.5) * mm});
            skLineSegment(sketch, "E47.9.30.0", {"start": v(0.75, -78.5) * mm, "end": v(-0.75, -78.5) * mm});
            skLineSegment(sketch, "E47.1.31.0", {"start": v(8.95, -78) * mm, "end": v(10.2, -89.93) * mm});
            skLineSegment(sketch, "E47.3.31.0", {"start": v(10.2, -89.93) * mm, "end": v(8.71, -90.08) * mm});
            skLineSegment(sketch, "E47.6.31.0", {"start": v(7.46, -78.15) * mm, "end": v(8.71, -90.08) * mm});
            skLineSegment(sketch, "E47.9.31.0", {"start": v(8.95, -78) * mm, "end": v(7.46, -78.15) * mm});
            skLineSegment(sketch, "E47.1.32.0", {"start": v(17.05, -76.63) * mm, "end": v(19.55, -88.37) * mm});
            skLineSegment(sketch, "E47.3.32.0", {"start": v(19.55, -88.37) * mm, "end": v(18.08, -88.68) * mm});
            skLineSegment(sketch, "E47.6.32.0", {"start": v(15.59, -76.94) * mm, "end": v(18.08, -88.68) * mm});
            skLineSegment(sketch, "E47.9.32.0", {"start": v(17.05, -76.63) * mm, "end": v(15.59, -76.94) * mm});
            skLineSegment(sketch, "E47.1.33.0", {"start": v(24.97, -74.43) * mm, "end": v(28.68, -85.84) * mm});
            skLineSegment(sketch, "E47.3.33.0", {"start": v(28.68, -85.84) * mm, "end": v(27.25, -86.3) * mm});
            skLineSegment(sketch, "E47.6.33.0", {"start": v(23.54, -74.89) * mm, "end": v(27.25, -86.3) * mm});
            skLineSegment(sketch, "E47.9.33.0", {"start": v(24.97, -74.43) * mm, "end": v(23.54, -74.89) * mm});
            skLineSegment(sketch, "E47.1.34.0", {"start": v(32.61, -71.4) * mm, "end": v(37.5, -82.37) * mm});
            skLineSegment(sketch, "E47.3.34.0", {"start": v(37.5, -82.37) * mm, "end": v(36.12, -82.98) * mm});
            skLineSegment(sketch, "E47.6.34.0", {"start": v(31.24, -72.02) * mm, "end": v(36.12, -82.98) * mm});
            skLineSegment(sketch, "E47.9.34.0", {"start": v(32.61, -71.4) * mm, "end": v(31.24, -72.02) * mm});
            skLineSegment(sketch, "E47.1.35.0", {"start": v(39.9, -67.6) * mm, "end": v(45.9, -78) * mm});
            skLineSegment(sketch, "E47.3.35.0", {"start": v(45.9, -78) * mm, "end": v(44.6, -78.75) * mm});
            skLineSegment(sketch, "E47.6.35.0", {"start": v(38.6, -68.36) * mm, "end": v(44.6, -78.75) * mm});
            skLineSegment(sketch, "E47.9.35.0", {"start": v(39.9, -67.6) * mm, "end": v(38.6, -68.36) * mm});
            skLineSegment(sketch, "E47.1.36.0", {"start": v(46.75, -63.07) * mm, "end": v(53.8, -72.78) * mm});
            skLineSegment(sketch, "E47.3.36.0", {"start": v(53.8, -72.78) * mm, "end": v(52.59, -73.66) * mm});
            skLineSegment(sketch, "E47.6.36.0", {"start": v(45.53, -63.95) * mm, "end": v(52.59, -73.66) * mm});
            skLineSegment(sketch, "E47.9.36.0", {"start": v(46.75, -63.07) * mm, "end": v(45.53, -63.95) * mm});
            skLineSegment(sketch, "E47.1.37.0", {"start": v(53.08, -57.84) * mm, "end": v(61.11, -66.75) * mm});
            skLineSegment(sketch, "E47.3.37.0", {"start": v(61.11, -66.75) * mm, "end": v(60, -67.76) * mm});
            skLineSegment(sketch, "E47.6.37.0", {"start": v(51.97, -58.84) * mm, "end": v(60, -67.76) * mm});
            skLineSegment(sketch, "E47.9.37.0", {"start": v(53.08, -57.84) * mm, "end": v(51.97, -58.84) * mm});
            skLineSegment(sketch, "E47.1.38.0", {"start": v(58.84, -51.97) * mm, "end": v(67.76, -60) * mm});
            skLineSegment(sketch, "E47.3.38.0", {"start": v(67.76, -60) * mm, "end": v(66.75, -61.11) * mm});
            skLineSegment(sketch, "E47.6.38.0", {"start": v(57.84, -53.08) * mm, "end": v(66.75, -61.11) * mm});
            skLineSegment(sketch, "E47.9.38.0", {"start": v(58.84, -51.97) * mm, "end": v(57.84, -53.08) * mm});
            skLineSegment(sketch, "E47.1.39.0", {"start": v(63.95, -45.53) * mm, "end": v(73.66, -52.59) * mm});
            skLineSegment(sketch, "E47.3.39.0", {"start": v(73.66, -52.59) * mm, "end": v(72.78, -53.8) * mm});
            skLineSegment(sketch, "E47.6.39.0", {"start": v(63.07, -46.75) * mm, "end": v(72.78, -53.8) * mm});
            skLineSegment(sketch, "E47.9.39.0", {"start": v(63.95, -45.53) * mm, "end": v(63.07, -46.75) * mm});
            skLineSegment(sketch, "E47.1.40.0", {"start": v(68.36, -38.6) * mm, "end": v(78.75, -44.6) * mm});
            skLineSegment(sketch, "E47.3.40.0", {"start": v(78.75, -44.6) * mm, "end": v(78, -45.9) * mm});
            skLineSegment(sketch, "E47.6.40.0", {"start": v(67.6, -39.9) * mm, "end": v(78, -45.9) * mm});
            skLineSegment(sketch, "E47.9.40.0", {"start": v(68.36, -38.6) * mm, "end": v(67.6, -39.9) * mm});
            skLineSegment(sketch, "E47.1.41.0", {"start": v(72.02, -31.24) * mm, "end": v(82.98, -36.12) * mm});
            skLineSegment(sketch, "E47.3.41.0", {"start": v(82.98, -36.12) * mm, "end": v(82.37, -37.5) * mm});
            skLineSegment(sketch, "E47.6.41.0", {"start": v(71.4, -32.61) * mm, "end": v(82.37, -37.5) * mm});
            skLineSegment(sketch, "E47.9.41.0", {"start": v(72.02, -31.24) * mm, "end": v(71.4, -32.61) * mm});
            skLineSegment(sketch, "E47.1.42.0", {"start": v(74.89, -23.54) * mm, "end": v(86.3, -27.25) * mm});
            skLineSegment(sketch, "E47.3.42.0", {"start": v(86.3, -27.25) * mm, "end": v(85.84, -28.68) * mm});
            skLineSegment(sketch, "E47.6.42.0", {"start": v(74.43, -24.97) * mm, "end": v(85.84, -28.68) * mm});
            skLineSegment(sketch, "E47.9.42.0", {"start": v(74.89, -23.54) * mm, "end": v(74.43, -24.97) * mm});
            skLineSegment(sketch, "E47.1.43.0", {"start": v(76.94, -15.59) * mm, "end": v(88.68, -18.08) * mm});
            skLineSegment(sketch, "E47.3.43.0", {"start": v(88.68, -18.08) * mm, "end": v(88.37, -19.55) * mm});
            skLineSegment(sketch, "E47.6.43.0", {"start": v(76.63, -17.05) * mm, "end": v(88.37, -19.55) * mm});
            skLineSegment(sketch, "E47.9.43.0", {"start": v(76.94, -15.59) * mm, "end": v(76.63, -17.05) * mm});
            skLineSegment(sketch, "E47.1.44.0", {"start": v(78.15, -7.46) * mm, "end": v(90.08, -8.71) * mm});
            skLineSegment(sketch, "E47.3.44.0", {"start": v(90.08, -8.71) * mm, "end": v(89.93, -10.2) * mm});
            skLineSegment(sketch, "E47.6.44.0", {"start": v(78, -8.95) * mm, "end": v(89.93, -10.2) * mm});
            skLineSegment(sketch, "E47.9.44.0", {"start": v(78.15, -7.46) * mm, "end": v(78, -8.95) * mm});
            skLineSegment(sketch, "E47.1.45.0", {"start": v(78.5, 0.75) * mm, "end": v(90.5, 0.75) * mm});
            skLineSegment(sketch, "E47.3.45.0", {"start": v(90.5, 0.75) * mm, "end": v(90.5, -0.75) * mm});
            skLineSegment(sketch, "E47.6.45.0", {"start": v(78.5, -0.75) * mm, "end": v(90.5, -0.75) * mm});
            skLineSegment(sketch, "E47.9.45.0", {"start": v(78.5, 0.75) * mm, "end": v(78.5, -0.75) * mm});
            skLineSegment(sketch, "E47.1.46.0", {"start": v(78, 8.95) * mm, "end": v(89.93, 10.2) * mm});
            skLineSegment(sketch, "E47.3.46.0", {"start": v(89.93, 10.2) * mm, "end": v(90.08, 8.71) * mm});
            skLineSegment(sketch, "E47.6.46.0", {"start": v(78.15, 7.46) * mm, "end": v(90.08, 8.71) * mm});
            skLineSegment(sketch, "E47.9.46.0", {"start": v(78, 8.95) * mm, "end": v(78.15, 7.46) * mm});
            skLineSegment(sketch, "E47.1.47.0", {"start": v(76.63, 17.05) * mm, "end": v(88.37, 19.55) * mm});
            skLineSegment(sketch, "E47.3.47.0", {"start": v(88.37, 19.55) * mm, "end": v(88.68, 18.08) * mm});
            skLineSegment(sketch, "E47.6.47.0", {"start": v(76.94, 15.59) * mm, "end": v(88.68, 18.08) * mm});
            skLineSegment(sketch, "E47.9.47.0", {"start": v(76.63, 17.05) * mm, "end": v(76.94, 15.59) * mm});
            skLineSegment(sketch, "E47.1.48.0", {"start": v(74.43, 24.97) * mm, "end": v(85.84, 28.68) * mm});
            skLineSegment(sketch, "E47.3.48.0", {"start": v(85.84, 28.68) * mm, "end": v(86.3, 27.25) * mm});
            skLineSegment(sketch, "E47.6.48.0", {"start": v(74.89, 23.54) * mm, "end": v(86.3, 27.25) * mm});
            skLineSegment(sketch, "E47.9.48.0", {"start": v(74.43, 24.97) * mm, "end": v(74.89, 23.54) * mm});
            skLineSegment(sketch, "E47.1.49.0", {"start": v(71.4, 32.61) * mm, "end": v(82.37, 37.5) * mm});
            skLineSegment(sketch, "E47.3.49.0", {"start": v(82.37, 37.5) * mm, "end": v(82.98, 36.12) * mm});
            skLineSegment(sketch, "E47.6.49.0", {"start": v(72.02, 31.24) * mm, "end": v(82.98, 36.12) * mm});
            skLineSegment(sketch, "E47.9.49.0", {"start": v(71.4, 32.61) * mm, "end": v(72.02, 31.24) * mm});
            skLineSegment(sketch, "E47.1.50.0", {"start": v(67.6, 39.9) * mm, "end": v(78, 45.9) * mm});
            skLineSegment(sketch, "E47.3.50.0", {"start": v(78, 45.9) * mm, "end": v(78.75, 44.6) * mm});
            skLineSegment(sketch, "E47.6.50.0", {"start": v(68.36, 38.6) * mm, "end": v(78.75, 44.6) * mm});
            skLineSegment(sketch, "E47.9.50.0", {"start": v(67.6, 39.9) * mm, "end": v(68.36, 38.6) * mm});
            skLineSegment(sketch, "E47.1.51.0", {"start": v(63.07, 46.75) * mm, "end": v(72.78, 53.8) * mm});
            skLineSegment(sketch, "E47.3.51.0", {"start": v(72.78, 53.8) * mm, "end": v(73.66, 52.59) * mm});
            skLineSegment(sketch, "E47.6.51.0", {"start": v(63.95, 45.53) * mm, "end": v(73.66, 52.59) * mm});
            skLineSegment(sketch, "E47.9.51.0", {"start": v(63.07, 46.75) * mm, "end": v(63.95, 45.53) * mm});
            skLineSegment(sketch, "E47.1.52.0", {"start": v(57.84, 53.08) * mm, "end": v(66.75, 61.11) * mm});
            skLineSegment(sketch, "E47.3.52.0", {"start": v(66.75, 61.11) * mm, "end": v(67.76, 60) * mm});
            skLineSegment(sketch, "E47.6.52.0", {"start": v(58.84, 51.97) * mm, "end": v(67.76, 60) * mm});
            skLineSegment(sketch, "E47.9.52.0", {"start": v(57.84, 53.08) * mm, "end": v(58.84, 51.97) * mm});
            skLineSegment(sketch, "E47.1.53.0", {"start": v(51.97, 58.84) * mm, "end": v(60, 67.76) * mm});
            skLineSegment(sketch, "E47.3.53.0", {"start": v(60, 67.76) * mm, "end": v(61.11, 66.75) * mm});
            skLineSegment(sketch, "E47.6.53.0", {"start": v(53.08, 57.84) * mm, "end": v(61.11, 66.75) * mm});
            skLineSegment(sketch, "E47.9.53.0", {"start": v(51.97, 58.84) * mm, "end": v(53.08, 57.84) * mm});
            skLineSegment(sketch, "E47.1.54.0", {"start": v(45.53, 63.95) * mm, "end": v(52.59, 73.66) * mm});
            skLineSegment(sketch, "E47.3.54.0", {"start": v(52.59, 73.66) * mm, "end": v(53.8, 72.78) * mm});
            skLineSegment(sketch, "E47.6.54.0", {"start": v(46.75, 63.07) * mm, "end": v(53.8, 72.78) * mm});
            skLineSegment(sketch, "E47.9.54.0", {"start": v(45.53, 63.95) * mm, "end": v(46.75, 63.07) * mm});
            skLineSegment(sketch, "E47.1.55.0", {"start": v(38.6, 68.36) * mm, "end": v(44.6, 78.75) * mm});
            skLineSegment(sketch, "E47.3.55.0", {"start": v(44.6, 78.75) * mm, "end": v(45.9, 78) * mm});
            skLineSegment(sketch, "E47.6.55.0", {"start": v(39.9, 67.6) * mm, "end": v(45.9, 78) * mm});
            skLineSegment(sketch, "E47.9.55.0", {"start": v(38.6, 68.36) * mm, "end": v(39.9, 67.6) * mm});
            skLineSegment(sketch, "E47.1.56.0", {"start": v(31.24, 72.02) * mm, "end": v(36.12, 82.98) * mm});
            skLineSegment(sketch, "E47.3.56.0", {"start": v(36.12, 82.98) * mm, "end": v(37.5, 82.37) * mm});
            skLineSegment(sketch, "E47.6.56.0", {"start": v(32.61, 71.4) * mm, "end": v(37.5, 82.37) * mm});
            skLineSegment(sketch, "E47.9.56.0", {"start": v(31.24, 72.02) * mm, "end": v(32.61, 71.4) * mm});
            skLineSegment(sketch, "E47.1.57.0", {"start": v(23.54, 74.89) * mm, "end": v(27.25, 86.3) * mm});
            skLineSegment(sketch, "E47.3.57.0", {"start": v(27.25, 86.3) * mm, "end": v(28.68, 85.84) * mm});
            skLineSegment(sketch, "E47.6.57.0", {"start": v(24.97, 74.43) * mm, "end": v(28.68, 85.84) * mm});
            skLineSegment(sketch, "E47.9.57.0", {"start": v(23.54, 74.89) * mm, "end": v(24.97, 74.43) * mm});
            skLineSegment(sketch, "E47.1.58.0", {"start": v(15.59, 76.94) * mm, "end": v(18.08, 88.68) * mm});
            skLineSegment(sketch, "E47.3.58.0", {"start": v(18.08, 88.68) * mm, "end": v(19.55, 88.37) * mm});
            skLineSegment(sketch, "E47.6.58.0", {"start": v(17.05, 76.63) * mm, "end": v(19.55, 88.37) * mm});
            skLineSegment(sketch, "E47.9.58.0", {"start": v(15.59, 76.94) * mm, "end": v(17.05, 76.63) * mm});
            skLineSegment(sketch, "E47.1.59.0", {"start": v(7.46, 78.15) * mm, "end": v(8.71, 90.08) * mm});
            skLineSegment(sketch, "E47.3.59.0", {"start": v(8.71, 90.08) * mm, "end": v(10.2, 89.93) * mm});
            skLineSegment(sketch, "E47.6.59.0", {"start": v(8.95, 78) * mm, "end": v(10.2, 89.93) * mm});
            skLineSegment(sketch, "E47.9.59.0", {"start": v(7.46, 78.15) * mm, "end": v(8.95, 78) * mm});
            skSolve(sketch);
        }
        {
            var Q0;
            Q0 = qSketchRegion(id + "F27", true);
            extrude(context, id + "F28", {"entities" : qUnion([Q0]), "operationType" : NewBodyOperationType.REMOVE, "oppositeDirection" : true, "depth" : 0.2 * mm, "offsetDistance" : 25 * mm});
        }
        {
            var Q0;
            Q0=makeQuery(id+"F26.boolean.opBoolean","COPY",FACE,{"derivedFrom":makeQuery(id+"F26.opExtrude","CAP_FACE",FACE,{"disambiguationData":[OSD([sQuery(id+"F25.wireOp",EDGE,"E42.bottom"),sQuery(id+"F25.wireOp",EDGE,"E42.top"),sQuery(id+"F25.wireOp",EDGE,"E42.left"),sQuery(id+"F25.wireOp",EDGE,"E42.right")])],"isStart":false})});
            extrude(context, id + "F29", {"entities" : qUnion([Q0]), "depth" : 1 * mm, "offsetDistance" : 25 * mm});
        }
        {
            var Q0;
            Q0=makeQuery(id+"F28.boolean.opBoolean","COPY",FACE,{"derivedFrom":makeQuery(id+"F28.opExtrude","CAP_FACE",FACE,{"disambiguationData":[OSD([sQuery(id+"F27.wireOp",EDGE,"E47.1.59.0"),sQuery(id+"F27.wireOp",EDGE,"E47.3.59.0"),sQuery(id+"F27.wireOp",EDGE,"E47.6.59.0"),sQuery(id+"F27.wireOp",EDGE,"E47.9.59.0")])],"isStart":false})});
            extrude(context, id + "F30", {"entities" : qUnion([Q0]), "depth" : 0.4 * mm, "offsetDistance" : 25 * mm});
        }
        {
            var Q0;
            Q0=makeQuery(id+"F15.opExtrude","CAP_FACE",FACE,{"disambiguationData":[OSD([sQuery(id+"F14.wireOp",EDGE,"E21.0"),sQuery(id+"F14.wireOp",EDGE,"E22"),sQuery(id+"F14.wireOp",EDGE,"E23"),sQuery(id+"F14.wireOp",EDGE,"E24"),sQuery(id+"F14.wireOp",EDGE,"E25.MirrorCS"),sQuery(id+"F14.wireOp",EDGE,"E26.MirrorCS"),sQuery(id+"F14.wireOp",EDGE,"E27.1.0"),sQuery(id+"F14.wireOp",EDGE,"E27.1.1"),sQuery(id+"F14.wireOp",EDGE,"E27.1.2"),sQuery(id+"F14.wireOp",EDGE,"E27.1.3"),sQuery(id+"F14.wireOp",EDGE,"E27.2.0"),sQuery(id+"F14.wireOp",EDGE,"E27.2.1"),sQuery(id+"F14.wireOp",EDGE,"E27.2.2"),sQuery(id+"F14.wireOp",EDGE,"E27.2.3"),sQuery(id+"F14.wireOp",EDGE,"E28.2.3.0"),sQuery(id+"F14.wireOp",EDGE,"E28.3.3.0"),sQuery(id+"F14.wireOp",EDGE,"E28.6.3.0"),sQuery(id+"F14.wireOp",EDGE,"E28.9.3.0"),sQuery(id+"F14.wireOp",EDGE,"E28.2.4.0"),sQuery(id+"F14.wireOp",EDGE,"E28.3.4.0"),sQuery(id+"F14.wireOp",EDGE,"E28.6.4.0"),sQuery(id+"F14.wireOp",EDGE,"E28.9.4.0"),sQuery(id+"F14.wireOp",EDGE,"E28.2.5.0"),sQuery(id+"F14.wireOp",EDGE,"E28.3.5.0"),sQuery(id+"F14.wireOp",EDGE,"E28.6.5.0"),sQuery(id+"F14.wireOp",EDGE,"E28.9.5.0"),sQuery(id+"F14.wireOp",EDGE,"E28.2.6.0"),sQuery(id+"F14.wireOp",EDGE,"E28.3.6.0"),sQuery(id+"F14.wireOp",EDGE,"E28.6.6.0"),sQuery(id+"F14.wireOp",EDGE,"E28.9.6.0"),sQuery(id+"F14.wireOp",EDGE,"E28.2.7.0"),sQuery(id+"F14.wireOp",EDGE,"E28.3.7.0"),sQuery(id+"F14.wireOp",EDGE,"E28.6.7.0"),sQuery(id+"F14.wireOp",EDGE,"E28.9.7.0"),sQuery(id+"F14.wireOp",EDGE,"E28.2.8.0"),sQuery(id+"F14.wireOp",EDGE,"E28.3.8.0"),sQuery(id+"F14.wireOp",EDGE,"E28.6.8.0"),sQuery(id+"F14.wireOp",EDGE,"E28.9.8.0"),sQuery(id+"F14.wireOp",EDGE,"E28.2.9.0"),sQuery(id+"F14.wireOp",EDGE,"E28.3.9.0"),sQuery(id+"F14.wireOp",EDGE,"E28.6.9.0"),sQuery(id+"F14.wireOp",EDGE,"E28.9.9.0"),sQuery(id+"F14.wireOp",EDGE,"E28.2.10.0"),sQuery(id+"F14.wireOp",EDGE,"E28.3.10.0"),sQuery(id+"F14.wireOp",EDGE,"E28.6.10.0"),sQuery(id+"F14.wireOp",EDGE,"E28.9.10.0"),sQuery(id+"F14.wireOp",EDGE,"E28.2.11.0"),sQuery(id+"F14.wireOp",EDGE,"E28.3.11.0"),sQuery(id+"F14.wireOp",EDGE,"E28.6.11.0"),sQuery(id+"F14.wireOp",EDGE,"E28.9.11.0"),sQuery(id+"F14.wireOp",EDGE,"E28.2.12.0"),sQuery(id+"F14.wireOp",EDGE,"E28.3.12.0"),sQuery(id+"F14.wireOp",EDGE,"E28.6.12.0"),sQuery(id+"F14.wireOp",EDGE,"E28.9.12.0"),sQuery(id+"F14.wireOp",EDGE,"E28.2.13.0"),sQuery(id+"F14.wireOp",EDGE,"E28.3.13.0"),sQuery(id+"F14.wireOp",EDGE,"E28.6.13.0"),sQuery(id+"F14.wireOp",EDGE,"E28.9.13.0"),sQuery(id+"F14.wireOp",EDGE,"E28.2.14.0"),sQuery(id+"F14.wireOp",EDGE,"E28.3.14.0"),sQuery(id+"F14.wireOp",EDGE,"E28.6.14.0"),sQuery(id+"F14.wireOp",EDGE,"E28.9.14.0"),sQuery(id+"F14.wireOp",EDGE,"E28.2.15.0"),sQuery(id+"F14.wireOp",EDGE,"E28.3.15.0"),sQuery(id+"F14.wireOp",EDGE,"E28.6.15.0"),sQuery(id+"F14.wireOp",EDGE,"E28.9.15.0"),sQuery(id+"F14.wireOp",EDGE,"E28.2.16.0"),sQuery(id+"F14.wireOp",EDGE,"E28.3.16.0"),sQuery(id+"F14.wireOp",EDGE,"E28.6.16.0"),sQuery(id+"F14.wireOp",EDGE,"E28.9.16.0"),sQuery(id+"F14.wireOp",EDGE,"E28.2.17.0"),sQuery(id+"F14.wireOp",EDGE,"E28.3.17.0"),sQuery(id+"F14.wireOp",EDGE,"E28.6.17.0"),sQuery(id+"F14.wireOp",EDGE,"E28.9.17.0"),sQuery(id+"F14.wireOp",EDGE,"E28.2.18.0"),sQuery(id+"F14.wireOp",EDGE,"E28.3.18.0"),sQuery(id+"F14.wireOp",EDGE,"E28.6.18.0"),sQuery(id+"F14.wireOp",EDGE,"E28.9.18.0"),sQuery(id+"F14.wireOp",EDGE,"E28.2.19.0"),sQuery(id+"F14.wireOp",EDGE,"E28.3.19.0"),sQuery(id+"F14.wireOp",EDGE,"E28.6.19.0"),sQuery(id+"F14.wireOp",EDGE,"E28.9.19.0"),sQuery(id+"F14.wireOp",EDGE,"E28.2.20.0"),sQuery(id+"F14.wireOp",EDGE,"E28.3.20.0"),sQuery(id+"F14.wireOp",EDGE,"E28.6.20.0"),sQuery(id+"F14.wireOp",EDGE,"E28.9.20.0"),sQuery(id+"F14.wireOp",EDGE,"E28.2.21.0"),sQuery(id+"F14.wireOp",EDGE,"E28.3.21.0"),sQuery(id+"F14.wireOp",EDGE,"E28.6.21.0"),sQuery(id+"F14.wireOp",EDGE,"E28.9.21.0"),sQuery(id+"F14.wireOp",EDGE,"E28.2.22.0"),sQuery(id+"F14.wireOp",EDGE,"E28.3.22.0"),sQuery(id+"F14.wireOp",EDGE,"E28.6.22.0"),sQuery(id+"F14.wireOp",EDGE,"E28.9.22.0"),sQuery(id+"F14.wireOp",EDGE,"E28.2.23.0"),sQuery(id+"F14.wireOp",EDGE,"E28.3.23.0"),sQuery(id+"F14.wireOp",EDGE,"E28.6.23.0"),sQuery(id+"F14.wireOp",EDGE,"E28.9.23.0"),sQuery(id+"F14.wireOp",EDGE,"E28.2.24.0"),sQuery(id+"F14.wireOp",EDGE,"E28.3.24.0"),sQuery(id+"F14.wireOp",EDGE,"E28.6.24.0"),sQuery(id+"F14.wireOp",EDGE,"E28.9.24.0"),sQuery(id+"F14.wireOp",EDGE,"E28.2.25.0"),sQuery(id+"F14.wireOp",EDGE,"E28.3.25.0"),sQuery(id+"F14.wireOp",EDGE,"E28.6.25.0"),sQuery(id+"F14.wireOp",EDGE,"E28.9.25.0"),sQuery(id+"F14.wireOp",EDGE,"E28.2.26.0"),sQuery(id+"F14.wireOp",EDGE,"E28.3.26.0"),sQuery(id+"F14.wireOp",EDGE,"E28.6.26.0"),sQuery(id+"F14.wireOp",EDGE,"E28.9.26.0"),sQuery(id+"F14.wireOp",EDGE,"E28.2.27.0"),sQuery(id+"F14.wireOp",EDGE,"E28.3.27.0"),sQuery(id+"F14.wireOp",EDGE,"E28.6.27.0"),sQuery(id+"F14.wireOp",EDGE,"E28.9.27.0"),sQuery(id+"F14.wireOp",EDGE,"E28.2.28.0"),sQuery(id+"F14.wireOp",EDGE,"E28.3.28.0"),sQuery(id+"F14.wireOp",EDGE,"E28.6.28.0"),sQuery(id+"F14.wireOp",EDGE,"E28.9.28.0"),sQuery(id+"F14.wireOp",EDGE,"E28.2.29.0"),sQuery(id+"F14.wireOp",EDGE,"E28.3.29.0"),sQuery(id+"F14.wireOp",EDGE,"E28.6.29.0"),sQuery(id+"F14.wireOp",EDGE,"E28.9.29.0"),sQuery(id+"F14.wireOp",EDGE,"E28.2.30.0"),sQuery(id+"F14.wireOp",EDGE,"E28.3.30.0"),sQuery(id+"F14.wireOp",EDGE,"E28.6.30.0"),sQuery(id+"F14.wireOp",EDGE,"E28.9.30.0"),sQuery(id+"F14.wireOp",EDGE,"E28.2.31.0"),sQuery(id+"F14.wireOp",EDGE,"E28.3.31.0"),sQuery(id+"F14.wireOp",EDGE,"E28.6.31.0"),sQuery(id+"F14.wireOp",EDGE,"E28.9.31.0"),sQuery(id+"F14.wireOp",EDGE,"E28.2.32.0"),sQuery(id+"F14.wireOp",EDGE,"E28.3.32.0"),sQuery(id+"F14.wireOp",EDGE,"E28.6.32.0"),sQuery(id+"F14.wireOp",EDGE,"E28.9.32.0"),sQuery(id+"F14.wireOp",EDGE,"E28.2.33.0"),sQuery(id+"F14.wireOp",EDGE,"E28.3.33.0"),sQuery(id+"F14.wireOp",EDGE,"E28.6.33.0"),sQuery(id+"F14.wireOp",EDGE,"E28.9.33.0"),sQuery(id+"F14.wireOp",EDGE,"E28.2.34.0"),sQuery(id+"F14.wireOp",EDGE,"E28.3.34.0"),sQuery(id+"F14.wireOp",EDGE,"E28.6.34.0"),sQuery(id+"F14.wireOp",EDGE,"E28.9.34.0"),sQuery(id+"F14.wireOp",EDGE,"E28.2.35.0"),sQuery(id+"F14.wireOp",EDGE,"E28.3.35.0"),sQuery(id+"F14.wireOp",EDGE,"E28.6.35.0"),sQuery(id+"F14.wireOp",EDGE,"E28.9.35.0"),sQuery(id+"F14.wireOp",EDGE,"E28.2.36.0"),sQuery(id+"F14.wireOp",EDGE,"E28.3.36.0"),sQuery(id+"F14.wireOp",EDGE,"E28.6.36.0"),sQuery(id+"F14.wireOp",EDGE,"E28.9.36.0"),sQuery(id+"F14.wireOp",EDGE,"E28.2.37.0"),sQuery(id+"F14.wireOp",EDGE,"E28.3.37.0"),sQuery(id+"F14.wireOp",EDGE,"E28.6.37.0"),sQuery(id+"F14.wireOp",EDGE,"E28.9.37.0"),sQuery(id+"F14.wireOp",EDGE,"E28.2.38.0"),sQuery(id+"F14.wireOp",EDGE,"E28.3.38.0"),sQuery(id+"F14.wireOp",EDGE,"E28.6.38.0"),sQuery(id+"F14.wireOp",EDGE,"E28.9.38.0"),sQuery(id+"F14.wireOp",EDGE,"E28.2.39.0"),sQuery(id+"F14.wireOp",EDGE,"E28.3.39.0"),sQuery(id+"F14.wireOp",EDGE,"E28.6.39.0"),sQuery(id+"F14.wireOp",EDGE,"E28.9.39.0")])],"isStart":false});
            var sketch = newSketch(context, id + "F31", { "sketchPlane" : qUnion([Q0])});
            skCircle(sketch, "E48.0", {"center": v(0, 0) * mm, "radius": 3 * mm});
            skCircle(sketch, "E49.0", {"center": v(0, 0) * mm, "radius": 5 * mm});
            skSolve(sketch);
        }
        {
            var Q0;
            Q0 = qSketchRegion(id + "F31", true);
            extrude(context, id + "F32", {"entities" : qUnion([Q0]), "operationType" : NewBodyOperationType.ADD, "depth" : 5 * mm, "offsetDistance" : 25 * mm});
        }
        {
            var Q0;
            Q0=makeQuery(id+"F32.opExtrude","CAP_FACE",FACE,{"disambiguationData":[OSD([sQuery(id+"F31.wireOp",EDGE,"E48.0"),sQuery(id+"F31.wireOp",EDGE,"E49.0")])],"isStart":false});
            var sketch = newSketch(context, id + "F33", { "sketchPlane" : qUnion([Q0])});
            skCircle(sketch, "E50.0.0", {"center": v(0, 0) * mm, "radius": 3 * mm});
            skCircle(sketch, "E51.0", {"center": v(0, 0) * mm, "radius": 5 * mm});
            skLineSegment(sketch, "E52", {"start": v(0, 50) * mm, "end": v(1.5, 50) * mm});
            skLineSegment(sketch, "E53", {"start": v(1.5, 50) * mm, "end": v(3, 4) * mm});
            skLineSegment(sketch, "E54.MirrorCS", {"start": v(0, 50) * mm, "end": v(-1.5, 50) * mm});
            skLineSegment(sketch, "E55.MirrorCS", {"start": v(-1.5, 50) * mm, "end": v(-3, 4) * mm});
            skSolve(sketch);
        }
        {
            var Q0;
            Q0 = qSketchRegion(id + "F33", true);
            extrude(context, id + "F34", {"entities" : qUnion([Q0]), "operationType" : NewBodyOperationType.ADD, "depth" : 1 * mm, "offsetDistance" : 25 * mm});
        }
        {
            var Q0;
            Q0=makeQuery(id+"F6.opExtrude","CAP_FACE",FACE,{"disambiguationData":[OSD([sQuery(id+"F0.wireOp",EDGE,"E0")])],"isStart":false});
            var sketch = newSketch(context, id + "F35", { "sketchPlane" : qUnion([Q0])});
            skCircle(sketch, "E56", {"center": v(0, 0) * mm, "radius": 5 * mm});
            skLineSegment(sketch, "E57", {"start": v(0, 80) * mm, "end": v(0.5, 80) * mm});
            skLineSegment(sketch, "E58", {"start": v(0.5, 80) * mm, "end": v(2, 4.58) * mm});
            skLineSegment(sketch, "E59.MirrorCS", {"start": v(0, 80) * mm, "end": v(-0.5, 80) * mm});
            skLineSegment(sketch, "E60.MirrorCS", {"start": v(-0.5, 80) * mm, "end": v(-2, 4.58) * mm});
            skSolve(sketch);
        }
        {
            var Q0;
            Q0 = qSketchRegion(id + "F35", true);
            extrude(context, id + "F36", {"entities" : qUnion([Q0]), "operationType" : NewBodyOperationType.ADD, "oppositeDirection" : true, "depth" : 1 * mm, "offsetDistance" : 25 * mm});
        }
    });
